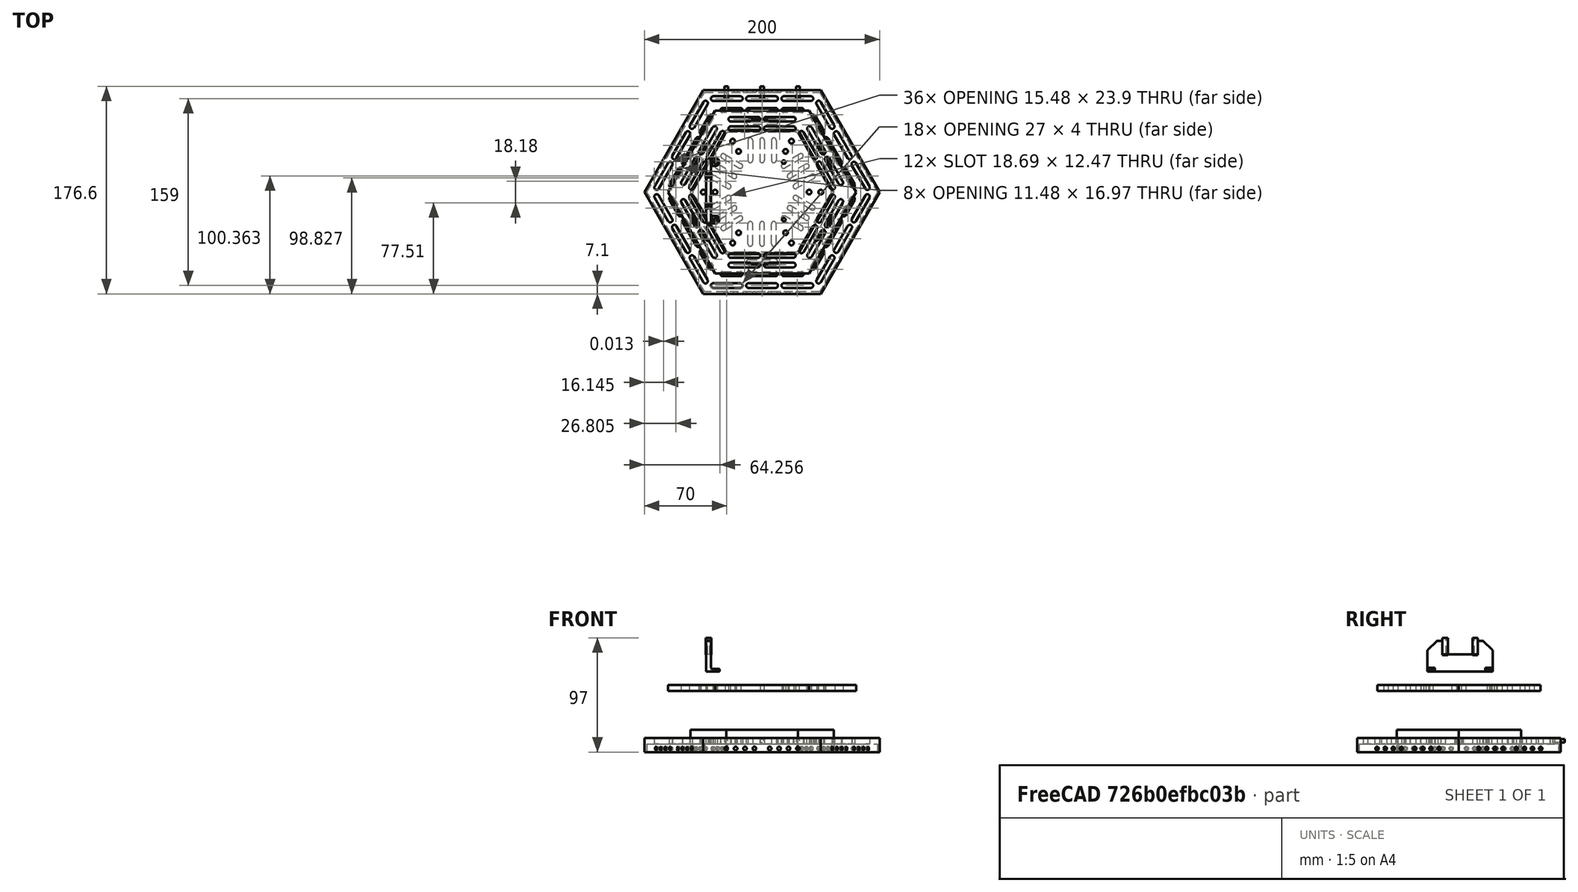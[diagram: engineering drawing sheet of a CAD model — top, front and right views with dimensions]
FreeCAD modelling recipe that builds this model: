
FCSTD DOCUMENT  (FreeCAD 0.16R)
Label: printable_ein
License: All rights reserved
LicenseURL: http://en.wikipedia.org/wiki/All_rights_reserved
objects: Part::Cylinder×299, Part::MultiFuse×130, Part::Box×90, Part::Cut×11, Part::Extrusion×6, Part::RegularPolygon×5, Part::Chamfer×5, App::MeasureDistance×2, Part::Fillet×2, Mesh::Feature×1
note: 548 computed .brp shape members not serialized (recipe doc carries the construction recipe); baked Part::Feature solids carry a one-line shape summary decoded from their .brp

FEATURE [Part::RegularPolygon] RegularPolygon  label="Polígono regular"
  Circumradius = 100
  Polygon = 6
FEATURE [Part::Extrusion] Extrude
  Base = -> RegularPolygon
  Dir = (0,0,12)
  Placement = pos=(0,0,-5) rot=(0,0,1;0rad)
  Solid = true
FEATURE [Part::RegularPolygon] RegularPolygon001  label="Polígono regular001"
  Circumradius = 61
  Polygon = 6
FEATURE [Part::Extrusion] Extrude001
  Base = -> RegularPolygon001
  Dir = (0,0,12)
  Solid = true
FEATURE [Part::Extrusion] Extrude002
  Base = -> RegularPolygon001
  Dir = (0,0,12)
  Solid = true
FEATURE [Part::RegularPolygon] RegularPolygon002  label="Polígono regular002"
  Circumradius = 59
  Polygon = 6
FEATURE [Part::Extrusion] Extrude003
  Base = -> RegularPolygon002
  Dir = (0,0,12)
  Solid = true
FEATURE [Part::Cut] Cut
  Base = -> Extrude002
  Tool = -> Extrude003
FEATURE [Part::RegularPolygon] RegularPolygon003  label="Polígono regular003"
  Circumradius = 98
  Polygon = 6
FEATURE [Part::Extrusion] Extrude004
  Base = -> RegularPolygon003
  Dir = (0,0,12)
  Solid = true
FEATURE [Part::Cut] Cut001
  Base = -> Extrude004
  Tool = -> Cut
FEATURE [Part::Cut] Cut002
  Base = -> Extrude
  Tool = -> Cut001
FEATURE [App::MeasureDistance] Distance  label="Distance: 65.9391 mm"
  Distance = 65.9391
  P1 = (-65.9695,0.0527623,7)
  P2 = (-33,57.1577,7)
FEATURE [App::MeasureDistance] Distance001  label="Distance: 99.9869 mm"
  Distance = 99.9869
  P1 = (-99.9935,0.0113197,7)
  P2 = (-50,86.6025,7)
FEATURE [Part::Cylinder] Cylinder  label="Cilindro"
  Angle = 360
  Height = 10
  Placement = pos=(0,90,2.5) rot=(1,0,0;1.5708rad)
  Radius = 1.5
FEATURE [Part::Cylinder] Cylinder001  label="Cilindro001"
  Angle = 360
  Height = 10
  Placement = pos=(6.5,90,2.5) rot=(1,0,0;1.5708rad)
  Radius = 1.5
FEATURE [Part::Cylinder] Cylinder002  label="Cilindro002"
  Angle = 360
  Height = 10
  Placement = pos=(14.5,90,2.5) rot=(1,0,0;1.5708rad)
  Radius = 1.5
FEATURE [Part::Cylinder] Cylinder003  label="Cilindro003"
  Angle = 360
  Height = 10
  Placement = pos=(14.5,90,2.5) rot=(1,0,0;1.5708rad)
  Radius = 1.5
FEATURE [Part::Cylinder] Cylinder004  label="Cilindro004"
  Angle = 360
  Height = 10
  Placement = pos=(22.5,90,2.5) rot=(1,0,0;1.5708rad)
  Radius = 1.5
FEATURE [Part::Cylinder] Cylinder005  label="Cilindro005"
  Angle = 360
  Height = 10
  Placement = pos=(30.5,90,2.5) rot=(1,0,0;1.5708rad)
  Radius = 1.5
FEATURE [Part::Cylinder] Cylinder006  label="Cilindro006"
  Angle = 360
  Height = 10
  Placement = pos=(-6.5,90,2.5) rot=(1,0,0;1.5708rad)
  Radius = 1.5
FEATURE [Part::Cylinder] Cylinder007  label="Cilindro007"
  Angle = 360
  Height = 10
  Placement = pos=(-14.5,90,2.5) rot=(1,0,0;1.5708rad)
  Radius = 1.5
FEATURE [Part::Cylinder] Cylinder008  label="Cilindro008"
  Angle = 360
  Height = 10
  Placement = pos=(-22.5,90,2.5) rot=(1,0,0;1.5708rad)
  Radius = 1.5
FEATURE [Part::Cylinder] Cylinder009  label="Cilindro009"
  Angle = 360
  Height = 10
  Placement = pos=(-30.5,90,2.5) rot=(1,0,0;1.5708rad)
  Radius = 1.5
FEATURE [Part::MultiFuse] Fusion
  Shapes = -> [Cylinder009,Cylinder008,Cylinder007,Cylinder006,Cylinder005,Cylinder003,Cylinder004,Cylinder002,Cylinder001]
FEATURE [Part::Cylinder] Cylinder010  label="Cilindro010"
  Angle = 360
  Height = 10
  Placement = pos=(6.5,90,2.5) rot=(1,0,0;1.5708rad)
  Radius = 1.5
FEATURE [Part::Cylinder] Cylinder011  label="Cilindro011"
  Angle = 360
  Height = 10
  Placement = pos=(14.5,90,2.5) rot=(1,0,0;1.5708rad)
  Radius = 1.5
FEATURE [Part::Cylinder] Cylinder012  label="Cilindro012"
  Angle = 360
  Height = 10
  Placement = pos=(14.5,90,2.5) rot=(1,0,0;1.5708rad)
  Radius = 1.5
FEATURE [Part::Cylinder] Cylinder013  label="Cilindro013"
  Angle = 360
  Height = 10
  Placement = pos=(22.5,90,2.5) rot=(1,0,0;1.5708rad)
  Radius = 1.5
FEATURE [Part::Cylinder] Cylinder014  label="Cilindro014"
  Angle = 360
  Height = 10
  Placement = pos=(30.5,90,2.5) rot=(1,0,0;1.5708rad)
  Radius = 1.5
FEATURE [Part::Cylinder] Cylinder015  label="Cilindro015"
  Angle = 360
  Height = 10
  Placement = pos=(-6.5,90,2.5) rot=(1,0,0;1.5708rad)
  Radius = 1.5
FEATURE [Part::Cylinder] Cylinder016  label="Cilindro016"
  Angle = 360
  Height = 10
  Placement = pos=(-14.5,90,2.5) rot=(1,0,0;1.5708rad)
  Radius = 1.5
FEATURE [Part::Cylinder] Cylinder017  label="Cilindro017"
  Angle = 360
  Height = 10
  Placement = pos=(-22.5,90,2.5) rot=(1,0,0;1.5708rad)
  Radius = 1.5
FEATURE [Part::Cylinder] Cylinder018  label="Cilindro018"
  Angle = 360
  Height = 10
  Placement = pos=(-30.5,90,2.5) rot=(1,0,0;1.5708rad)
  Radius = 1.5
FEATURE [Part::MultiFuse] Fusion001
  Placement = pos=(0,-29,0) rot=(0,0,1;0rad)
  Shapes = -> [Cylinder017,Cylinder016,Cylinder015,Cylinder012,Cylinder013,Cylinder011,Cylinder010]
FEATURE [Part::MultiFuse] Fusion002
  Shapes = -> [Fusion,Fusion001]
FEATURE [Part::Cylinder] Cylinder019  label="Cilindro019"
  Angle = 360
  Height = 10
  Placement = pos=(6.5,90,2.5) rot=(1,0,0;1.5708rad)
  Radius = 1.5
FEATURE [Part::Cylinder] Cylinder020  label="Cilindro020"
  Angle = 360
  Height = 10
  Placement = pos=(14.5,90,2.5) rot=(1,0,0;1.5708rad)
  Radius = 1.5
FEATURE [Part::Cylinder] Cylinder021  label="Cilindro021"
  Angle = 360
  Height = 10
  Placement = pos=(14.5,90,2.5) rot=(1,0,0;1.5708rad)
  Radius = 1.5
FEATURE [Part::Cylinder] Cylinder022  label="Cilindro022"
  Angle = 360
  Height = 10
  Placement = pos=(22.5,90,2.5) rot=(1,0,0;1.5708rad)
  Radius = 1.5
FEATURE [Part::Cylinder] Cylinder023  label="Cilindro023"
  Angle = 360
  Height = 10
  Placement = pos=(30.5,90,2.5) rot=(1,0,0;1.5708rad)
  Radius = 1.5
FEATURE [Part::Cylinder] Cylinder024  label="Cilindro024"
  Angle = 360
  Height = 10
  Placement = pos=(-6.5,90,2.5) rot=(1,0,0;1.5708rad)
  Radius = 1.5
FEATURE [Part::Cylinder] Cylinder025  label="Cilindro025"
  Angle = 360
  Height = 10
  Placement = pos=(-14.5,90,2.5) rot=(1,0,0;1.5708rad)
  Radius = 1.5
FEATURE [Part::Cylinder] Cylinder026  label="Cilindro026"
  Angle = 360
  Height = 10
  Placement = pos=(-22.5,90,2.5) rot=(1,0,0;1.5708rad)
  Radius = 1.5
FEATURE [Part::Cylinder] Cylinder027  label="Cilindro027"
  Angle = 360
  Height = 10
  Placement = pos=(-30.5,90,2.5) rot=(1,0,0;1.5708rad)
  Radius = 1.5
FEATURE [Part::MultiFuse] Fusion003
  Shapes = -> [Cylinder027,Cylinder026,Cylinder025,Cylinder024,Cylinder023,Cylinder021,Cylinder022,Cylinder020,Cylinder019]
FEATURE [Part::Cylinder] Cylinder028  label="Cilindro028"
  Angle = 360
  Height = 10
  Placement = pos=(6.5,90,2.5) rot=(1,0,0;1.5708rad)
  Radius = 1.5
FEATURE [Part::Cylinder] Cylinder029  label="Cilindro029"
  Angle = 360
  Height = 10
  Placement = pos=(14.5,90,2.5) rot=(1,0,0;1.5708rad)
  Radius = 1.5
FEATURE [Part::Cylinder] Cylinder030  label="Cilindro030"
  Angle = 360
  Height = 10
  Placement = pos=(14.5,90,2.5) rot=(1,0,0;1.5708rad)
  Radius = 1.5
FEATURE [Part::Cylinder] Cylinder031  label="Cilindro031"
  Angle = 360
  Height = 10
  Placement = pos=(22.5,90,2.5) rot=(1,0,0;1.5708rad)
  Radius = 1.5
FEATURE [Part::Cylinder] Cylinder032  label="Cilindro032"
  Angle = 360
  Height = 10
  Placement = pos=(-6.5,90,2.5) rot=(1,0,0;1.5708rad)
  Radius = 1.5
FEATURE [Part::Cylinder] Cylinder033  label="Cilindro033"
  Angle = 360
  Height = 10
  Placement = pos=(-14.5,90,2.5) rot=(1,0,0;1.5708rad)
  Radius = 1.5
FEATURE [Part::Cylinder] Cylinder034  label="Cilindro034"
  Angle = 360
  Height = 10
  Placement = pos=(-22.5,90,2.5) rot=(1,0,0;1.5708rad)
  Radius = 1.5
FEATURE [Part::MultiFuse] Fusion004
  Placement = pos=(0,-29,0) rot=(0,0,1;0rad)
  Shapes = -> [Cylinder034,Cylinder033,Cylinder032,Cylinder030,Cylinder031,Cylinder029,Cylinder028]
FEATURE [Part::MultiFuse] Fusion005
  Placement = pos=(0,0,0) rot=(0,0,1;1.0472rad)
  Shapes = -> [Fusion003,Fusion004]
FEATURE [Part::Cylinder] Cylinder035  label="Cilindro035"
  Angle = 360
  Height = 10
  Placement = pos=(6.5,90,2.5) rot=(1,0,0;1.5708rad)
  Radius = 1.5
FEATURE [Part::Cylinder] Cylinder036  label="Cilindro036"
  Angle = 360
  Height = 10
  Placement = pos=(14.5,90,2.5) rot=(1,0,0;1.5708rad)
  Radius = 1.5
FEATURE [Part::Cylinder] Cylinder037  label="Cilindro037"
  Angle = 360
  Height = 10
  Placement = pos=(14.5,90,2.5) rot=(1,0,0;1.5708rad)
  Radius = 1.5
FEATURE [Part::Cylinder] Cylinder038  label="Cilindro038"
  Angle = 360
  Height = 10
  Placement = pos=(22.5,90,2.5) rot=(1,0,0;1.5708rad)
  Radius = 1.5
FEATURE [Part::Cylinder] Cylinder039  label="Cilindro039"
  Angle = 360
  Height = 10
  Placement = pos=(30.5,90,2.5) rot=(1,0,0;1.5708rad)
  Radius = 1.5
FEATURE [Part::Cylinder] Cylinder040  label="Cilindro040"
  Angle = 360
  Height = 10
  Placement = pos=(-6.5,90,2.5) rot=(1,0,0;1.5708rad)
  Radius = 1.5
FEATURE [Part::Cylinder] Cylinder041  label="Cilindro041"
  Angle = 360
  Height = 10
  Placement = pos=(-14.5,90,2.5) rot=(1,0,0;1.5708rad)
  Radius = 1.5
FEATURE [Part::Cylinder] Cylinder042  label="Cilindro042"
  Angle = 360
  Height = 10
  Placement = pos=(-22.5,90,2.5) rot=(1,0,0;1.5708rad)
  Radius = 1.5
FEATURE [Part::Cylinder] Cylinder043  label="Cilindro043"
  Angle = 360
  Height = 10
  Placement = pos=(-30.5,90,2.5) rot=(1,0,0;1.5708rad)
  Radius = 1.5
FEATURE [Part::MultiFuse] Fusion006
  Shapes = -> [Cylinder043,Cylinder042,Cylinder041,Cylinder040,Cylinder039,Cylinder037,Cylinder038,Cylinder036,Cylinder035]
FEATURE [Part::Cylinder] Cylinder044  label="Cilindro044"
  Angle = 360
  Height = 10
  Placement = pos=(6.5,90,2.5) rot=(1,0,0;1.5708rad)
  Radius = 1.5
FEATURE [Part::Cylinder] Cylinder045  label="Cilindro045"
  Angle = 360
  Height = 10
  Placement = pos=(14.5,90,2.5) rot=(1,0,0;1.5708rad)
  Radius = 1.5
FEATURE [Part::Cylinder] Cylinder046  label="Cilindro046"
  Angle = 360
  Height = 10
  Placement = pos=(14.5,90,2.5) rot=(1,0,0;1.5708rad)
  Radius = 1.5
FEATURE [Part::Cylinder] Cylinder047  label="Cilindro047"
  Angle = 360
  Height = 10
  Placement = pos=(22.5,90,2.5) rot=(1,0,0;1.5708rad)
  Radius = 1.5
FEATURE [Part::Cylinder] Cylinder048  label="Cilindro048"
  Angle = 360
  Height = 10
  Placement = pos=(-6.5,90,2.5) rot=(1,0,0;1.5708rad)
  Radius = 1.5
FEATURE [Part::Cylinder] Cylinder049  label="Cilindro049"
  Angle = 360
  Height = 10
  Placement = pos=(-14.5,90,2.5) rot=(1,0,0;1.5708rad)
  Radius = 1.5
FEATURE [Part::Cylinder] Cylinder050  label="Cilindro050"
  Angle = 360
  Height = 10
  Placement = pos=(-22.5,90,2.5) rot=(1,0,0;1.5708rad)
  Radius = 1.5
FEATURE [Part::MultiFuse] Fusion007
  Placement = pos=(0,-29,0) rot=(0,0,1;0rad)
  Shapes = -> [Cylinder050,Cylinder049,Cylinder048,Cylinder046,Cylinder047,Cylinder045,Cylinder044]
FEATURE [Part::MultiFuse] Fusion008
  Placement = pos=(0,0,0) rot=(0,0,1;2.0944rad)
  Shapes = -> [Fusion006,Fusion007]
FEATURE [Part::Cylinder] Cylinder051  label="Cilindro051"
  Angle = 360
  Height = 10
  Placement = pos=(6.5,90,2.5) rot=(1,0,0;1.5708rad)
  Radius = 1.5
FEATURE [Part::Cylinder] Cylinder052  label="Cilindro052"
  Angle = 360
  Height = 10
  Placement = pos=(14.5,90,2.5) rot=(1,0,0;1.5708rad)
  Radius = 1.5
FEATURE [Part::Cylinder] Cylinder053  label="Cilindro053"
  Angle = 360
  Height = 10
  Placement = pos=(14.5,90,2.5) rot=(1,0,0;1.5708rad)
  Radius = 1.5
FEATURE [Part::Cylinder] Cylinder054  label="Cilindro054"
  Angle = 360
  Height = 10
  Placement = pos=(22.5,90,2.5) rot=(1,0,0;1.5708rad)
  Radius = 1.5
FEATURE [Part::Cylinder] Cylinder055  label="Cilindro055"
  Angle = 360
  Height = 10
  Placement = pos=(30.5,90,2.5) rot=(1,0,0;1.5708rad)
  Radius = 1.5
FEATURE [Part::Cylinder] Cylinder056  label="Cilindro056"
  Angle = 360
  Height = 10
  Placement = pos=(-6.5,90,2.5) rot=(1,0,0;1.5708rad)
  Radius = 1.5
FEATURE [Part::Cylinder] Cylinder057  label="Cilindro057"
  Angle = 360
  Height = 10
  Placement = pos=(-14.5,90,2.5) rot=(1,0,0;1.5708rad)
  Radius = 1.5
FEATURE [Part::Cylinder] Cylinder058  label="Cilindro058"
  Angle = 360
  Height = 10
  Placement = pos=(-22.5,90,2.5) rot=(1,0,0;1.5708rad)
  Radius = 1.5
FEATURE [Part::Cylinder] Cylinder059  label="Cilindro059"
  Angle = 360
  Height = 10
  Placement = pos=(-30.5,90,2.5) rot=(1,0,0;1.5708rad)
  Radius = 1.5
FEATURE [Part::MultiFuse] Fusion009
  Shapes = -> [Cylinder059,Cylinder058,Cylinder057,Cylinder056,Cylinder055,Cylinder053,Cylinder054,Cylinder052,Cylinder051]
FEATURE [Part::Cylinder] Cylinder060  label="Cilindro060"
  Angle = 360
  Height = 10
  Placement = pos=(6.5,90,2.5) rot=(1,0,0;1.5708rad)
  Radius = 1.5
FEATURE [Part::Cylinder] Cylinder061  label="Cilindro061"
  Angle = 360
  Height = 10
  Placement = pos=(14.5,90,2.5) rot=(1,0,0;1.5708rad)
  Radius = 1.5
FEATURE [Part::Cylinder] Cylinder062  label="Cilindro062"
  Angle = 360
  Height = 10
  Placement = pos=(14.5,90,2.5) rot=(1,0,0;1.5708rad)
  Radius = 1.5
FEATURE [Part::Cylinder] Cylinder063  label="Cilindro063"
  Angle = 360
  Height = 10
  Placement = pos=(22.5,90,2.5) rot=(1,0,0;1.5708rad)
  Radius = 1.5
FEATURE [Part::Cylinder] Cylinder064  label="Cilindro064"
  Angle = 360
  Height = 10
  Placement = pos=(-6.5,90,2.5) rot=(1,0,0;1.5708rad)
  Radius = 1.5
FEATURE [Part::Cylinder] Cylinder065  label="Cilindro065"
  Angle = 360
  Height = 10
  Placement = pos=(-14.5,90,2.5) rot=(1,0,0;1.5708rad)
  Radius = 1.5
FEATURE [Part::Cylinder] Cylinder066  label="Cilindro066"
  Angle = 360
  Height = 10
  Placement = pos=(-22.5,90,2.5) rot=(1,0,0;1.5708rad)
  Radius = 1.5
FEATURE [Part::MultiFuse] Fusion010
  Placement = pos=(0,-29,0) rot=(0,0,1;0rad)
  Shapes = -> [Cylinder066,Cylinder065,Cylinder064,Cylinder062,Cylinder063,Cylinder061,Cylinder060]
FEATURE [Part::MultiFuse] Fusion011
  Placement = pos=(0,0,0) rot=(0,0,1;3.14159rad)
  Shapes = -> [Fusion009,Fusion010]
FEATURE [Part::Cylinder] Cylinder067  label="Cilindro067"
  Angle = 360
  Height = 10
  Placement = pos=(6.5,90,2.5) rot=(1,0,0;1.5708rad)
  Radius = 1.5
FEATURE [Part::Cylinder] Cylinder068  label="Cilindro068"
  Angle = 360
  Height = 10
  Placement = pos=(14.5,90,2.5) rot=(1,0,0;1.5708rad)
  Radius = 1.5
FEATURE [Part::Cylinder] Cylinder069  label="Cilindro069"
  Angle = 360
  Height = 10
  Placement = pos=(14.5,90,2.5) rot=(1,0,0;1.5708rad)
  Radius = 1.5
FEATURE [Part::Cylinder] Cylinder070  label="Cilindro070"
  Angle = 360
  Height = 10
  Placement = pos=(22.5,90,2.5) rot=(1,0,0;1.5708rad)
  Radius = 1.5
FEATURE [Part::Cylinder] Cylinder071  label="Cilindro071"
  Angle = 360
  Height = 10
  Placement = pos=(30.5,90,2.5) rot=(1,0,0;1.5708rad)
  Radius = 1.5
FEATURE [Part::Cylinder] Cylinder072  label="Cilindro072"
  Angle = 360
  Height = 10
  Placement = pos=(-6.5,90,2.5) rot=(1,0,0;1.5708rad)
  Radius = 1.5
FEATURE [Part::Cylinder] Cylinder073  label="Cilindro073"
  Angle = 360
  Height = 10
  Placement = pos=(-14.5,90,2.5) rot=(1,0,0;1.5708rad)
  Radius = 1.5
FEATURE [Part::Cylinder] Cylinder074  label="Cilindro074"
  Angle = 360
  Height = 10
  Placement = pos=(-22.5,90,2.5) rot=(1,0,0;1.5708rad)
  Radius = 1.5
FEATURE [Part::Cylinder] Cylinder075  label="Cilindro075"
  Angle = 360
  Height = 10
  Placement = pos=(-30.5,90,2.5) rot=(1,0,0;1.5708rad)
  Radius = 1.5
FEATURE [Part::MultiFuse] Fusion012
  Shapes = -> [Cylinder075,Cylinder074,Cylinder073,Cylinder072,Cylinder071,Cylinder069,Cylinder070,Cylinder068,Cylinder067]
FEATURE [Part::Cylinder] Cylinder076  label="Cilindro076"
  Angle = 360
  Height = 10
  Placement = pos=(6.5,90,2.5) rot=(1,0,0;1.5708rad)
  Radius = 1.5
FEATURE [Part::Cylinder] Cylinder077  label="Cilindro077"
  Angle = 360
  Height = 10
  Placement = pos=(14.5,90,2.5) rot=(1,0,0;1.5708rad)
  Radius = 1.5
FEATURE [Part::Cylinder] Cylinder078  label="Cilindro078"
  Angle = 360
  Height = 10
  Placement = pos=(14.5,90,2.5) rot=(1,0,0;1.5708rad)
  Radius = 1.5
FEATURE [Part::Cylinder] Cylinder079  label="Cilindro079"
  Angle = 360
  Height = 10
  Placement = pos=(22.5,90,2.5) rot=(1,0,0;1.5708rad)
  Radius = 1.5
FEATURE [Part::Cylinder] Cylinder080  label="Cilindro080"
  Angle = 360
  Height = 10
  Placement = pos=(-6.5,90,2.5) rot=(1,0,0;1.5708rad)
  Radius = 1.5
FEATURE [Part::Cylinder] Cylinder081  label="Cilindro081"
  Angle = 360
  Height = 10
  Placement = pos=(-14.5,90,2.5) rot=(1,0,0;1.5708rad)
  Radius = 1.5
FEATURE [Part::Cylinder] Cylinder082  label="Cilindro082"
  Angle = 360
  Height = 10
  Placement = pos=(-22.5,90,2.5) rot=(1,0,0;1.5708rad)
  Radius = 1.5
FEATURE [Part::MultiFuse] Fusion013
  Placement = pos=(0,-29,0) rot=(0,0,1;0rad)
  Shapes = -> [Cylinder082,Cylinder081,Cylinder080,Cylinder078,Cylinder079,Cylinder077,Cylinder076]
FEATURE [Part::MultiFuse] Fusion014
  Placement = pos=(0,0,0) rot=(0,0,-1;1.0472rad)
  Shapes = -> [Fusion012,Fusion013]
FEATURE [Part::Cylinder] Cylinder083  label="Cilindro083"
  Angle = 360
  Height = 10
  Placement = pos=(6.5,90,2.5) rot=(1,0,0;1.5708rad)
  Radius = 1.5
FEATURE [Part::Cylinder] Cylinder084  label="Cilindro084"
  Angle = 360
  Height = 10
  Placement = pos=(14.5,90,2.5) rot=(1,0,0;1.5708rad)
  Radius = 1.5
FEATURE [Part::Cylinder] Cylinder085  label="Cilindro085"
  Angle = 360
  Height = 10
  Placement = pos=(14.5,90,2.5) rot=(1,0,0;1.5708rad)
  Radius = 1.5
FEATURE [Part::Cylinder] Cylinder086  label="Cilindro086"
  Angle = 360
  Height = 10
  Placement = pos=(22.5,90,2.5) rot=(1,0,0;1.5708rad)
  Radius = 1.5
FEATURE [Part::Cylinder] Cylinder087  label="Cilindro087"
  Angle = 360
  Height = 10
  Placement = pos=(30.5,90,2.5) rot=(1,0,0;1.5708rad)
  Radius = 1.5
FEATURE [Part::Cylinder] Cylinder088  label="Cilindro088"
  Angle = 360
  Height = 10
  Placement = pos=(-6.5,90,2.5) rot=(1,0,0;1.5708rad)
  Radius = 1.5
FEATURE [Part::Cylinder] Cylinder089  label="Cilindro089"
  Angle = 360
  Height = 10
  Placement = pos=(-14.5,90,2.5) rot=(1,0,0;1.5708rad)
  Radius = 1.5
FEATURE [Part::Cylinder] Cylinder090  label="Cilindro090"
  Angle = 360
  Height = 10
  Placement = pos=(-22.5,90,2.5) rot=(1,0,0;1.5708rad)
  Radius = 1.5
FEATURE [Part::Cylinder] Cylinder091  label="Cilindro091"
  Angle = 360
  Height = 10
  Placement = pos=(-30.5,90,2.5) rot=(1,0,0;1.5708rad)
  Radius = 1.5
FEATURE [Part::MultiFuse] Fusion015
  Shapes = -> [Cylinder091,Cylinder090,Cylinder089,Cylinder088,Cylinder087,Cylinder085,Cylinder086,Cylinder084,Cylinder083]
FEATURE [Part::Cylinder] Cylinder092  label="Cilindro092"
  Angle = 360
  Height = 10
  Placement = pos=(6.5,90,2.5) rot=(1,0,0;1.5708rad)
  Radius = 1.5
FEATURE [Part::Cylinder] Cylinder093  label="Cilindro093"
  Angle = 360
  Height = 10
  Placement = pos=(14.5,90,2.5) rot=(1,0,0;1.5708rad)
  Radius = 1.5
FEATURE [Part::Cylinder] Cylinder094  label="Cilindro094"
  Angle = 360
  Height = 10
  Placement = pos=(14.5,90,2.5) rot=(1,0,0;1.5708rad)
  Radius = 1.5
FEATURE [Part::Cylinder] Cylinder095  label="Cilindro095"
  Angle = 360
  Height = 10
  Placement = pos=(22.5,90,2.5) rot=(1,0,0;1.5708rad)
  Radius = 1.5
FEATURE [Part::Cylinder] Cylinder096  label="Cilindro096"
  Angle = 360
  Height = 10
  Placement = pos=(-6.5,90,2.5) rot=(1,0,0;1.5708rad)
  Radius = 1.5
FEATURE [Part::Cylinder] Cylinder097  label="Cilindro097"
  Angle = 360
  Height = 10
  Placement = pos=(-14.5,90,2.5) rot=(1,0,0;1.5708rad)
  Radius = 1.5
FEATURE [Part::Cylinder] Cylinder098  label="Cilindro098"
  Angle = 360
  Height = 10
  Placement = pos=(-22.5,90,2.5) rot=(1,0,0;1.5708rad)
  Radius = 1.5
FEATURE [Part::MultiFuse] Fusion016
  Placement = pos=(0,-29,0) rot=(0,0,1;0rad)
  Shapes = -> [Cylinder098,Cylinder097,Cylinder096,Cylinder094,Cylinder095,Cylinder093,Cylinder092]
FEATURE [Part::MultiFuse] Fusion017
  Placement = pos=(0,0,0) rot=(0,0,-1;2.0944rad)
  Shapes = -> [Fusion015,Fusion016]
FEATURE [Part::MultiFuse] Fusion018
  Placement = pos=(0,0,1.5) rot=(0,0,1;0rad)
  Shapes = -> [Fusion017,Fusion014,Fusion011,Fusion008,Fusion005,Fusion002]
FEATURE [Part::Cut] Cut003
  Base = -> Cut002
  Tool = -> Fusion018
FEATURE [Part::Box] Box  label="Cubo"
  Height = 10
  Length = 23
  Width = 4
FEATURE [Part::Cylinder] Cylinder099  label="Cilindro099"
  Angle = 360
  Height = 10
  Placement = pos=(0,2,0) rot=(0,0,1;0rad)
  Radius = 2
FEATURE [Part::Cylinder] Cylinder100  label="Cilindro100"
  Angle = 360
  Height = 10
  Placement = pos=(23,2,0) rot=(0,0,1;0rad)
  Radius = 2
FEATURE [Part::MultiFuse] Fusion019
  Placement = pos=(-11.5,77.5,0) rot=(0,0,1;0rad)
  Shapes = -> [Cylinder099,Cylinder100,Box]
FEATURE [Part::Box] Box001  label="Cubo001"
  Height = 10
  Length = 23
  Width = 4
FEATURE [Part::Cylinder] Cylinder101  label="Cilindro101"
  Angle = 360
  Height = 10
  Placement = pos=(0,2,0) rot=(0,0,1;0rad)
  Radius = 2
FEATURE [Part::Cylinder] Cylinder102  label="Cilindro102"
  Angle = 360
  Height = 10
  Placement = pos=(23,2,0) rot=(0,0,1;0rad)
  Radius = 2
FEATURE [Part::MultiFuse] Fusion020
  Placement = pos=(-11.5,67.5,0) rot=(0,0,1;0rad)
  Shapes = -> [Cylinder101,Cylinder102,Box001]
FEATURE [Part::Box] Box002  label="Cubo002"
  Height = 10
  Length = 23
  Width = 4
FEATURE [Part::Cylinder] Cylinder103  label="Cilindro103"
  Angle = 360
  Height = 10
  Placement = pos=(0,2,0) rot=(0,0,1;0rad)
  Radius = 2
FEATURE [Part::Cylinder] Cylinder104  label="Cilindro104"
  Angle = 360
  Height = 10
  Placement = pos=(23,2,0) rot=(0,0,1;0rad)
  Radius = 2
FEATURE [Part::MultiFuse] Fusion021
  Placement = pos=(-11.5,57.5,0) rot=(0,0,1;0rad)
  Shapes = -> [Cylinder103,Cylinder104,Box002]
FEATURE [Part::Box] Box003  label="Cubo003"
  Height = 10
  Length = 23
  Width = 4
FEATURE [Part::Cylinder] Cylinder105  label="Cilindro105"
  Angle = 360
  Height = 10
  Placement = pos=(0,2,0) rot=(0,0,1;0rad)
  Radius = 2
FEATURE [Part::Cylinder] Cylinder106  label="Cilindro106"
  Angle = 360
  Height = 10
  Placement = pos=(23,2,0) rot=(0,0,1;0rad)
  Radius = 2
FEATURE [Part::MultiFuse] Fusion022
  Placement = pos=(18.5,77.5,0) rot=(0,0,1;0rad)
  Shapes = -> [Cylinder105,Cylinder106,Box003]
FEATURE [Part::Box] Box004  label="Cubo004"
  Height = 10
  Length = 23
  Width = 4
FEATURE [Part::Cylinder] Cylinder107  label="Cilindro107"
  Angle = 360
  Height = 10
  Placement = pos=(0,2,0) rot=(0,0,1;0rad)
  Radius = 2
FEATURE [Part::Cylinder] Cylinder108  label="Cilindro108"
  Angle = 360
  Height = 10
  Placement = pos=(23,2,0) rot=(0,0,1;0rad)
  Radius = 2
FEATURE [Part::MultiFuse] Fusion023
  Placement = pos=(-41.5,77.5,0) rot=(0,0,1;0rad)
  Shapes = -> [Cylinder107,Cylinder108,Box004]
FEATURE [Mesh::Feature] raspy3b
  Placement = pos=(-43,-27,60) rot=(1,0,0;1.5708rad)
FEATURE [Part::Box] Box005  label="Cubo005"
  Height = 10
  Length = 15
  Width = 4
FEATURE [Part::Cylinder] Cylinder109  label="Cilindro109"
  Angle = 360
  Height = 10
  Placement = pos=(0,2,0) rot=(0,0,1;0rad)
  Radius = 2
FEATURE [Part::Cylinder] Cylinder110  label="Cilindro110"
  Angle = 360
  Height = 10
  Placement = pos=(15,2,0) rot=(0,0,1;0rad)
  Radius = 2
FEATURE [Part::MultiFuse] Fusion024
  Placement = pos=(18.5,67.5,0) rot=(0,0,1;0rad)
  Shapes = -> [Box005,Cylinder110,Cylinder109]
FEATURE [Part::Box] Box006  label="Cubo006"
  Height = 10
  Length = 15
  Width = 4
FEATURE [Part::Cylinder] Cylinder111  label="Cilindro111"
  Angle = 360
  Height = 10
  Placement = pos=(0,2,0) rot=(0,0,1;0rad)
  Radius = 2
FEATURE [Part::Cylinder] Cylinder112  label="Cilindro112"
  Angle = 360
  Height = 10
  Placement = pos=(15,2,0) rot=(0,0,1;0rad)
  Radius = 2
FEATURE [Part::MultiFuse] Fusion025
  Placement = pos=(-33.5,67.5,0) rot=(0,0,1;0rad)
  Shapes = -> [Box006,Cylinder112,Cylinder111]
FEATURE [Part::MultiFuse] Fusion026
  Shapes = -> [Fusion023,Fusion022,Fusion021,Fusion019,Fusion020,Fusion024,Fusion025]
FEATURE [Part::Box] Box007  label="Cubo007"
  Height = 10
  Length = 23
  Width = 4
FEATURE [Part::Cylinder] Cylinder113  label="Cilindro113"
  Angle = 360
  Height = 10
  Placement = pos=(0,2,0) rot=(0,0,1;0rad)
  Radius = 2
FEATURE [Part::Cylinder] Cylinder114  label="Cilindro114"
  Angle = 360
  Height = 10
  Placement = pos=(23,2,0) rot=(0,0,1;0rad)
  Radius = 2
FEATURE [Part::MultiFuse] Fusion027
  Placement = pos=(-11.5,77.5,0) rot=(0,0,1;0rad)
  Shapes = -> [Cylinder113,Cylinder114,Box007]
FEATURE [Part::Box] Box008  label="Cubo008"
  Height = 10
  Length = 23
  Width = 4
FEATURE [Part::Cylinder] Cylinder115  label="Cilindro115"
  Angle = 360
  Height = 10
  Placement = pos=(0,2,0) rot=(0,0,1;0rad)
  Radius = 2
FEATURE [Part::Cylinder] Cylinder116  label="Cilindro116"
  Angle = 360
  Height = 10
  Placement = pos=(23,2,0) rot=(0,0,1;0rad)
  Radius = 2
FEATURE [Part::MultiFuse] Fusion028
  Placement = pos=(-11.5,67.5,0) rot=(0,0,1;0rad)
  Shapes = -> [Cylinder115,Cylinder116,Box008]
FEATURE [Part::Box] Box009  label="Cubo009"
  Height = 10
  Length = 23
  Width = 4
FEATURE [Part::Cylinder] Cylinder117  label="Cilindro117"
  Angle = 360
  Height = 10
  Placement = pos=(0,2,0) rot=(0,0,1;0rad)
  Radius = 2
FEATURE [Part::Cylinder] Cylinder118  label="Cilindro118"
  Angle = 360
  Height = 10
  Placement = pos=(23,2,0) rot=(0,0,1;0rad)
  Radius = 2
FEATURE [Part::MultiFuse] Fusion029
  Placement = pos=(-11.5,57.5,0) rot=(0,0,1;0rad)
  Shapes = -> [Cylinder117,Cylinder118,Box009]
FEATURE [Part::Box] Box010  label="Cubo010"
  Height = 10
  Length = 23
  Width = 4
FEATURE [Part::Cylinder] Cylinder119  label="Cilindro119"
  Angle = 360
  Height = 10
  Placement = pos=(0,2,0) rot=(0,0,1;0rad)
  Radius = 2
FEATURE [Part::Cylinder] Cylinder120  label="Cilindro120"
  Angle = 360
  Height = 10
  Placement = pos=(23,2,0) rot=(0,0,1;0rad)
  Radius = 2
FEATURE [Part::MultiFuse] Fusion030
  Placement = pos=(18.5,77.5,0) rot=(0,0,1;0rad)
  Shapes = -> [Cylinder119,Cylinder120,Box010]
FEATURE [Part::Box] Box011  label="Cubo011"
  Height = 10
  Length = 23
  Width = 4
FEATURE [Part::Cylinder] Cylinder121  label="Cilindro121"
  Angle = 360
  Height = 10
  Placement = pos=(0,2,0) rot=(0,0,1;0rad)
  Radius = 2
FEATURE [Part::Cylinder] Cylinder122  label="Cilindro122"
  Angle = 360
  Height = 10
  Placement = pos=(23,2,0) rot=(0,0,1;0rad)
  Radius = 2
FEATURE [Part::MultiFuse] Fusion031
  Placement = pos=(-41.5,77.5,0) rot=(0,0,1;0rad)
  Shapes = -> [Cylinder121,Cylinder122,Box011]
FEATURE [Part::Box] Box012  label="Cubo012"
  Height = 10
  Length = 15
  Width = 4
FEATURE [Part::Cylinder] Cylinder123  label="Cilindro123"
  Angle = 360
  Height = 10
  Placement = pos=(0,2,0) rot=(0,0,1;0rad)
  Radius = 2
FEATURE [Part::Cylinder] Cylinder124  label="Cilindro124"
  Angle = 360
  Height = 10
  Placement = pos=(15,2,0) rot=(0,0,1;0rad)
  Radius = 2
FEATURE [Part::MultiFuse] Fusion032
  Placement = pos=(18.5,67.5,0) rot=(0,0,1;0rad)
  Shapes = -> [Box012,Cylinder124,Cylinder123]
FEATURE [Part::Box] Box013  label="Cubo013"
  Height = 10
  Length = 15
  Width = 4
FEATURE [Part::Cylinder] Cylinder125  label="Cilindro125"
  Angle = 360
  Height = 10
  Placement = pos=(0,2,0) rot=(0,0,1;0rad)
  Radius = 2
FEATURE [Part::Cylinder] Cylinder126  label="Cilindro126"
  Angle = 360
  Height = 10
  Placement = pos=(15,2,0) rot=(0,0,1;0rad)
  Radius = 2
FEATURE [Part::MultiFuse] Fusion033
  Placement = pos=(-33.5,67.5,0) rot=(0,0,1;0rad)
  Shapes = -> [Box013,Cylinder126,Cylinder125]
FEATURE [Part::MultiFuse] Fusion034
  Placement = pos=(0,0,0) rot=(0,0,1;1.0472rad)
  Shapes = -> [Fusion031,Fusion030,Fusion029,Fusion027,Fusion028,Fusion032,Fusion033]
FEATURE [Part::Box] Box014  label="Cubo014"
  Height = 10
  Length = 23
  Width = 4
FEATURE [Part::Cylinder] Cylinder127  label="Cilindro127"
  Angle = 360
  Height = 10
  Placement = pos=(0,2,0) rot=(0,0,1;0rad)
  Radius = 2
FEATURE [Part::Cylinder] Cylinder128  label="Cilindro128"
  Angle = 360
  Height = 10
  Placement = pos=(23,2,0) rot=(0,0,1;0rad)
  Radius = 2
FEATURE [Part::MultiFuse] Fusion035
  Placement = pos=(-11.5,77.5,0) rot=(0,0,1;0rad)
  Shapes = -> [Cylinder127,Cylinder128,Box014]
FEATURE [Part::Box] Box015  label="Cubo015"
  Height = 10
  Length = 23
  Width = 4
FEATURE [Part::Cylinder] Cylinder129  label="Cilindro129"
  Angle = 360
  Height = 10
  Placement = pos=(0,2,0) rot=(0,0,1;0rad)
  Radius = 2
FEATURE [Part::Cylinder] Cylinder130  label="Cilindro130"
  Angle = 360
  Height = 10
  Placement = pos=(23,2,0) rot=(0,0,1;0rad)
  Radius = 2
FEATURE [Part::MultiFuse] Fusion036
  Placement = pos=(-11.5,67.5,0) rot=(0,0,1;0rad)
  Shapes = -> [Cylinder129,Cylinder130,Box015]
FEATURE [Part::Box] Box016  label="Cubo016"
  Height = 10
  Length = 23
  Width = 4
FEATURE [Part::Cylinder] Cylinder131  label="Cilindro131"
  Angle = 360
  Height = 10
  Placement = pos=(0,2,0) rot=(0,0,1;0rad)
  Radius = 2
FEATURE [Part::Cylinder] Cylinder132  label="Cilindro132"
  Angle = 360
  Height = 10
  Placement = pos=(23,2,0) rot=(0,0,1;0rad)
  Radius = 2
FEATURE [Part::MultiFuse] Fusion037
  Placement = pos=(-11.5,57.5,0) rot=(0,0,1;0rad)
  Shapes = -> [Cylinder131,Cylinder132,Box016]
FEATURE [Part::Box] Box017  label="Cubo017"
  Height = 10
  Length = 23
  Width = 4
FEATURE [Part::Cylinder] Cylinder133  label="Cilindro133"
  Angle = 360
  Height = 10
  Placement = pos=(0,2,0) rot=(0,0,1;0rad)
  Radius = 2
FEATURE [Part::Cylinder] Cylinder134  label="Cilindro134"
  Angle = 360
  Height = 10
  Placement = pos=(23,2,0) rot=(0,0,1;0rad)
  Radius = 2
FEATURE [Part::MultiFuse] Fusion038
  Placement = pos=(18.5,77.5,0) rot=(0,0,1;0rad)
  Shapes = -> [Cylinder133,Cylinder134,Box017]
FEATURE [Part::Box] Box018  label="Cubo018"
  Height = 10
  Length = 23
  Width = 4
FEATURE [Part::Cylinder] Cylinder135  label="Cilindro135"
  Angle = 360
  Height = 10
  Placement = pos=(0,2,0) rot=(0,0,1;0rad)
  Radius = 2
FEATURE [Part::Cylinder] Cylinder136  label="Cilindro136"
  Angle = 360
  Height = 10
  Placement = pos=(23,2,0) rot=(0,0,1;0rad)
  Radius = 2
FEATURE [Part::MultiFuse] Fusion039
  Placement = pos=(-41.5,77.5,0) rot=(0,0,1;0rad)
  Shapes = -> [Cylinder135,Cylinder136,Box018]
FEATURE [Part::Box] Box019  label="Cubo019"
  Height = 10
  Length = 15
  Width = 4
FEATURE [Part::Cylinder] Cylinder137  label="Cilindro137"
  Angle = 360
  Height = 10
  Placement = pos=(0,2,0) rot=(0,0,1;0rad)
  Radius = 2
FEATURE [Part::Cylinder] Cylinder138  label="Cilindro138"
  Angle = 360
  Height = 10
  Placement = pos=(15,2,0) rot=(0,0,1;0rad)
  Radius = 2
FEATURE [Part::MultiFuse] Fusion040
  Placement = pos=(18.5,67.5,0) rot=(0,0,1;0rad)
  Shapes = -> [Box019,Cylinder138,Cylinder137]
FEATURE [Part::Box] Box020  label="Cubo020"
  Height = 10
  Length = 15
  Width = 4
FEATURE [Part::Cylinder] Cylinder139  label="Cilindro139"
  Angle = 360
  Height = 10
  Placement = pos=(0,2,0) rot=(0,0,1;0rad)
  Radius = 2
FEATURE [Part::Cylinder] Cylinder140  label="Cilindro140"
  Angle = 360
  Height = 10
  Placement = pos=(15,2,0) rot=(0,0,1;0rad)
  Radius = 2
FEATURE [Part::MultiFuse] Fusion041
  Placement = pos=(-33.5,67.5,0) rot=(0,0,1;0rad)
  Shapes = -> [Box020,Cylinder140,Cylinder139]
FEATURE [Part::MultiFuse] Fusion042
  Placement = pos=(0,0,0) rot=(0,0,-1;1.0472rad)
  Shapes = -> [Fusion039,Fusion038,Fusion037,Fusion035,Fusion036,Fusion040,Fusion041]
FEATURE [Part::Box] Box021  label="Cubo021"
  Height = 10
  Length = 23
  Width = 4
FEATURE [Part::Cylinder] Cylinder141  label="Cilindro141"
  Angle = 360
  Height = 10
  Placement = pos=(0,2,0) rot=(0,0,1;0rad)
  Radius = 2
FEATURE [Part::Cylinder] Cylinder142  label="Cilindro142"
  Angle = 360
  Height = 10
  Placement = pos=(23,2,0) rot=(0,0,1;0rad)
  Radius = 2
FEATURE [Part::MultiFuse] Fusion043
  Placement = pos=(-11.5,77.5,0) rot=(0,0,1;0rad)
  Shapes = -> [Cylinder141,Cylinder142,Box021]
FEATURE [Part::Box] Box022  label="Cubo022"
  Height = 10
  Length = 23
  Width = 4
FEATURE [Part::Cylinder] Cylinder143  label="Cilindro143"
  Angle = 360
  Height = 10
  Placement = pos=(0,2,0) rot=(0,0,1;0rad)
  Radius = 2
FEATURE [Part::Cylinder] Cylinder144  label="Cilindro144"
  Angle = 360
  Height = 10
  Placement = pos=(23,2,0) rot=(0,0,1;0rad)
  Radius = 2
FEATURE [Part::MultiFuse] Fusion044
  Placement = pos=(-11.5,67.5,0) rot=(0,0,1;0rad)
  Shapes = -> [Cylinder143,Cylinder144,Box022]
FEATURE [Part::Box] Box023  label="Cubo023"
  Height = 10
  Length = 23
  Width = 4
FEATURE [Part::Cylinder] Cylinder145  label="Cilindro145"
  Angle = 360
  Height = 10
  Placement = pos=(0,2,0) rot=(0,0,1;0rad)
  Radius = 2
FEATURE [Part::Cylinder] Cylinder146  label="Cilindro146"
  Angle = 360
  Height = 10
  Placement = pos=(23,2,0) rot=(0,0,1;0rad)
  Radius = 2
FEATURE [Part::MultiFuse] Fusion045
  Placement = pos=(-11.5,57.5,0) rot=(0,0,1;0rad)
  Shapes = -> [Cylinder145,Cylinder146,Box023]
FEATURE [Part::Box] Box024  label="Cubo024"
  Height = 10
  Length = 23
  Width = 4
FEATURE [Part::Cylinder] Cylinder147  label="Cilindro147"
  Angle = 360
  Height = 10
  Placement = pos=(0,2,0) rot=(0,0,1;0rad)
  Radius = 2
FEATURE [Part::Cylinder] Cylinder148  label="Cilindro148"
  Angle = 360
  Height = 10
  Placement = pos=(23,2,0) rot=(0,0,1;0rad)
  Radius = 2
FEATURE [Part::MultiFuse] Fusion046
  Placement = pos=(18.5,77.5,0) rot=(0,0,1;0rad)
  Shapes = -> [Cylinder147,Cylinder148,Box024]
FEATURE [Part::Box] Box025  label="Cubo025"
  Height = 10
  Length = 23
  Width = 4
FEATURE [Part::Cylinder] Cylinder149  label="Cilindro149"
  Angle = 360
  Height = 10
  Placement = pos=(0,2,0) rot=(0,0,1;0rad)
  Radius = 2
FEATURE [Part::Cylinder] Cylinder150  label="Cilindro150"
  Angle = 360
  Height = 10
  Placement = pos=(23,2,0) rot=(0,0,1;0rad)
  Radius = 2
FEATURE [Part::MultiFuse] Fusion047
  Placement = pos=(-41.5,77.5,0) rot=(0,0,1;0rad)
  Shapes = -> [Cylinder149,Cylinder150,Box025]
FEATURE [Part::Box] Box026  label="Cubo026"
  Height = 10
  Length = 15
  Width = 4
FEATURE [Part::Cylinder] Cylinder151  label="Cilindro151"
  Angle = 360
  Height = 10
  Placement = pos=(0,2,0) rot=(0,0,1;0rad)
  Radius = 2
FEATURE [Part::Cylinder] Cylinder152  label="Cilindro152"
  Angle = 360
  Height = 10
  Placement = pos=(15,2,0) rot=(0,0,1;0rad)
  Radius = 2
FEATURE [Part::MultiFuse] Fusion048
  Placement = pos=(18.5,67.5,0) rot=(0,0,1;0rad)
  Shapes = -> [Box026,Cylinder152,Cylinder151]
FEATURE [Part::Box] Box027  label="Cubo027"
  Height = 10
  Length = 15
  Width = 4
FEATURE [Part::Cylinder] Cylinder153  label="Cilindro153"
  Angle = 360
  Height = 10
  Placement = pos=(0,2,0) rot=(0,0,1;0rad)
  Radius = 2
FEATURE [Part::Cylinder] Cylinder154  label="Cilindro154"
  Angle = 360
  Height = 10
  Placement = pos=(15,2,0) rot=(0,0,1;0rad)
  Radius = 2
FEATURE [Part::MultiFuse] Fusion049
  Placement = pos=(-33.5,67.5,0) rot=(0,0,1;0rad)
  Shapes = -> [Box027,Cylinder154,Cylinder153]
FEATURE [Part::MultiFuse] Fusion050
  Placement = pos=(0,0,0) rot=(0,0,1;3.14159rad)
  Shapes = -> [Fusion047,Fusion046,Fusion045,Fusion043,Fusion044,Fusion048,Fusion049]
FEATURE [Part::Box] Box028  label="Cubo028"
  Height = 10
  Length = 23
  Width = 4
FEATURE [Part::Cylinder] Cylinder155  label="Cilindro155"
  Angle = 360
  Height = 10
  Placement = pos=(0,2,0) rot=(0,0,1;0rad)
  Radius = 2
FEATURE [Part::Cylinder] Cylinder156  label="Cilindro156"
  Angle = 360
  Height = 10
  Placement = pos=(23,2,0) rot=(0,0,1;0rad)
  Radius = 2
FEATURE [Part::MultiFuse] Fusion051
  Placement = pos=(-11.5,77.5,0) rot=(0,0,1;0rad)
  Shapes = -> [Cylinder155,Cylinder156,Box028]
FEATURE [Part::Box] Box029  label="Cubo029"
  Height = 10
  Length = 23
  Width = 4
FEATURE [Part::Cylinder] Cylinder157  label="Cilindro157"
  Angle = 360
  Height = 10
  Placement = pos=(0,2,0) rot=(0,0,1;0rad)
  Radius = 2
FEATURE [Part::Cylinder] Cylinder158  label="Cilindro158"
  Angle = 360
  Height = 10
  Placement = pos=(23,2,0) rot=(0,0,1;0rad)
  Radius = 2
FEATURE [Part::MultiFuse] Fusion052
  Placement = pos=(-11.5,67.5,0) rot=(0,0,1;0rad)
  Shapes = -> [Cylinder157,Cylinder158,Box029]
FEATURE [Part::Box] Box030  label="Cubo030"
  Height = 10
  Length = 23
  Width = 4
FEATURE [Part::Cylinder] Cylinder159  label="Cilindro159"
  Angle = 360
  Height = 10
  Placement = pos=(0,2,0) rot=(0,0,1;0rad)
  Radius = 2
FEATURE [Part::Cylinder] Cylinder160  label="Cilindro160"
  Angle = 360
  Height = 10
  Placement = pos=(23,2,0) rot=(0,0,1;0rad)
  Radius = 2
FEATURE [Part::MultiFuse] Fusion053
  Placement = pos=(-11.5,57.5,0) rot=(0,0,1;0rad)
  Shapes = -> [Cylinder159,Cylinder160,Box030]
FEATURE [Part::Box] Box031  label="Cubo031"
  Height = 10
  Length = 23
  Width = 4
FEATURE [Part::Cylinder] Cylinder161  label="Cilindro161"
  Angle = 360
  Height = 10
  Placement = pos=(0,2,0) rot=(0,0,1;0rad)
  Radius = 2
FEATURE [Part::Cylinder] Cylinder162  label="Cilindro162"
  Angle = 360
  Height = 10
  Placement = pos=(23,2,0) rot=(0,0,1;0rad)
  Radius = 2
FEATURE [Part::MultiFuse] Fusion054
  Placement = pos=(18.5,77.5,0) rot=(0,0,1;0rad)
  Shapes = -> [Cylinder161,Cylinder162,Box031]
FEATURE [Part::Box] Box032  label="Cubo032"
  Height = 10
  Length = 23
  Width = 4
FEATURE [Part::Cylinder] Cylinder163  label="Cilindro163"
  Angle = 360
  Height = 10
  Placement = pos=(0,2,0) rot=(0,0,1;0rad)
  Radius = 2
FEATURE [Part::Cylinder] Cylinder164  label="Cilindro164"
  Angle = 360
  Height = 10
  Placement = pos=(23,2,0) rot=(0,0,1;0rad)
  Radius = 2
FEATURE [Part::MultiFuse] Fusion055
  Placement = pos=(-41.5,77.5,0) rot=(0,0,1;0rad)
  Shapes = -> [Cylinder163,Cylinder164,Box032]
FEATURE [Part::Box] Box033  label="Cubo033"
  Height = 10
  Length = 15
  Width = 4
FEATURE [Part::Cylinder] Cylinder165  label="Cilindro165"
  Angle = 360
  Height = 10
  Placement = pos=(0,2,0) rot=(0,0,1;0rad)
  Radius = 2
FEATURE [Part::Cylinder] Cylinder166  label="Cilindro166"
  Angle = 360
  Height = 10
  Placement = pos=(15,2,0) rot=(0,0,1;0rad)
  Radius = 2
FEATURE [Part::MultiFuse] Fusion056
  Placement = pos=(18.5,67.5,0) rot=(0,0,1;0rad)
  Shapes = -> [Box033,Cylinder166,Cylinder165]
FEATURE [Part::Box] Box034  label="Cubo034"
  Height = 10
  Length = 15
  Width = 4
FEATURE [Part::Cylinder] Cylinder167  label="Cilindro167"
  Angle = 360
  Height = 10
  Placement = pos=(0,2,0) rot=(0,0,1;0rad)
  Radius = 2
FEATURE [Part::Cylinder] Cylinder168  label="Cilindro168"
  Angle = 360
  Height = 10
  Placement = pos=(15,2,0) rot=(0,0,1;0rad)
  Radius = 2
FEATURE [Part::MultiFuse] Fusion057
  Placement = pos=(-33.5,67.5,0) rot=(0,0,1;0rad)
  Shapes = -> [Box034,Cylinder168,Cylinder167]
FEATURE [Part::MultiFuse] Fusion058
  Placement = pos=(0,0,0) rot=(0,0,1;2.0944rad)
  Shapes = -> [Fusion055,Fusion054,Fusion053,Fusion051,Fusion052,Fusion056,Fusion057]
FEATURE [Part::Box] Box035  label="Cubo035"
  Height = 10
  Length = 23
  Width = 4
FEATURE [Part::Cylinder] Cylinder169  label="Cilindro169"
  Angle = 360
  Height = 10
  Placement = pos=(0,2,0) rot=(0,0,1;0rad)
  Radius = 2
FEATURE [Part::Cylinder] Cylinder170  label="Cilindro170"
  Angle = 360
  Height = 10
  Placement = pos=(23,2,0) rot=(0,0,1;0rad)
  Radius = 2
FEATURE [Part::MultiFuse] Fusion059
  Placement = pos=(-11.5,77.5,0) rot=(0,0,1;0rad)
  Shapes = -> [Cylinder169,Cylinder170,Box035]
FEATURE [Part::Box] Box036  label="Cubo036"
  Height = 10
  Length = 23
  Width = 4
FEATURE [Part::Cylinder] Cylinder171  label="Cilindro171"
  Angle = 360
  Height = 10
  Placement = pos=(0,2,0) rot=(0,0,1;0rad)
  Radius = 2
FEATURE [Part::Cylinder] Cylinder172  label="Cilindro172"
  Angle = 360
  Height = 10
  Placement = pos=(23,2,0) rot=(0,0,1;0rad)
  Radius = 2
FEATURE [Part::MultiFuse] Fusion060
  Placement = pos=(-11.5,67.5,0) rot=(0,0,1;0rad)
  Shapes = -> [Cylinder171,Cylinder172,Box036]
FEATURE [Part::Box] Box037  label="Cubo037"
  Height = 10
  Length = 23
  Width = 4
FEATURE [Part::Cylinder] Cylinder173  label="Cilindro173"
  Angle = 360
  Height = 10
  Placement = pos=(0,2,0) rot=(0,0,1;0rad)
  Radius = 2
FEATURE [Part::Cylinder] Cylinder174  label="Cilindro174"
  Angle = 360
  Height = 10
  Placement = pos=(23,2,0) rot=(0,0,1;0rad)
  Radius = 2
FEATURE [Part::MultiFuse] Fusion061
  Placement = pos=(-11.5,57.5,0) rot=(0,0,1;0rad)
  Shapes = -> [Cylinder173,Cylinder174,Box037]
FEATURE [Part::Box] Box038  label="Cubo038"
  Height = 10
  Length = 23
  Width = 4
FEATURE [Part::Cylinder] Cylinder175  label="Cilindro175"
  Angle = 360
  Height = 10
  Placement = pos=(0,2,0) rot=(0,0,1;0rad)
  Radius = 2
FEATURE [Part::Cylinder] Cylinder176  label="Cilindro176"
  Angle = 360
  Height = 10
  Placement = pos=(23,2,0) rot=(0,0,1;0rad)
  Radius = 2
FEATURE [Part::MultiFuse] Fusion062
  Placement = pos=(18.5,77.5,0) rot=(0,0,1;0rad)
  Shapes = -> [Cylinder175,Cylinder176,Box038]
FEATURE [Part::Box] Box039  label="Cubo039"
  Height = 10
  Length = 23
  Width = 4
FEATURE [Part::Cylinder] Cylinder177  label="Cilindro177"
  Angle = 360
  Height = 10
  Placement = pos=(0,2,0) rot=(0,0,1;0rad)
  Radius = 2
FEATURE [Part::Cylinder] Cylinder178  label="Cilindro178"
  Angle = 360
  Height = 10
  Placement = pos=(23,2,0) rot=(0,0,1;0rad)
  Radius = 2
FEATURE [Part::MultiFuse] Fusion063
  Placement = pos=(-41.5,77.5,0) rot=(0,0,1;0rad)
  Shapes = -> [Cylinder177,Cylinder178,Box039]
FEATURE [Part::Box] Box040  label="Cubo040"
  Height = 10
  Length = 15
  Width = 4
FEATURE [Part::Cylinder] Cylinder179  label="Cilindro179"
  Angle = 360
  Height = 10
  Placement = pos=(0,2,0) rot=(0,0,1;0rad)
  Radius = 2
FEATURE [Part::Cylinder] Cylinder180  label="Cilindro180"
  Angle = 360
  Height = 10
  Placement = pos=(15,2,0) rot=(0,0,1;0rad)
  Radius = 2
FEATURE [Part::MultiFuse] Fusion064
  Placement = pos=(18.5,67.5,0) rot=(0,0,1;0rad)
  Shapes = -> [Box040,Cylinder180,Cylinder179]
FEATURE [Part::Box] Box041  label="Cubo041"
  Height = 10
  Length = 15
  Width = 4
FEATURE [Part::Cylinder] Cylinder181  label="Cilindro181"
  Angle = 360
  Height = 10
  Placement = pos=(0,2,0) rot=(0,0,1;0rad)
  Radius = 2
FEATURE [Part::Cylinder] Cylinder182  label="Cilindro182"
  Angle = 360
  Height = 10
  Placement = pos=(15,2,0) rot=(0,0,1;0rad)
  Radius = 2
FEATURE [Part::MultiFuse] Fusion065
  Placement = pos=(-33.5,67.5,0) rot=(0,0,1;0rad)
  Shapes = -> [Box041,Cylinder182,Cylinder181]
FEATURE [Part::MultiFuse] Fusion066
  Placement = pos=(0,0,0) rot=(0,0,-1;2.0944rad)
  Shapes = -> [Fusion063,Fusion062,Fusion061,Fusion059,Fusion060,Fusion064,Fusion065]
FEATURE [Part::MultiFuse] Fusion067
  Placement = pos=(0,0,-7) rot=(0,0,1;0rad)
  Shapes = -> [Fusion026,Fusion034,Fusion042,Fusion050,Fusion058,Fusion066]
FEATURE [Part::Cut] Cut004
  Base = -> Cut003
  Tool = -> Fusion067
FEATURE [Part::Cylinder] Cylinder183  label="Cilindro183"
  Angle = 360
  Height = 10
  Placement = pos=(25,43.3,0) rot=(0,0,1;0rad)
  Radius = 2
FEATURE [Part::Cylinder] Cylinder184  label="Cilindro184"
  Angle = 360
  Height = 10
  Placement = pos=(20,34.6,0) rot=(0,0,1;0rad)
  Radius = 2
FEATURE [Part::Box] Box042  label="Cubo042"
  Height = 10
  Length = 4
  Width = 17
FEATURE [Part::Cylinder] Cylinder185  label="Cilindro185"
  Angle = 360
  Height = 10
  Placement = pos=(2,0,0) rot=(0,0,1;0rad)
  Radius = 2
FEATURE [Part::Cylinder] Cylinder186  label="Cilindro186"
  Angle = 360
  Height = 10
  Placement = pos=(2,17,0) rot=(0,0,1;0rad)
  Radius = 2
FEATURE [Part::MultiFuse] Fusion068
  Placement = pos=(-2,27,0) rot=(0,0,1;0rad)
  Shapes = -> [Cylinder186,Cylinder185,Box042]
FEATURE [Part::Box] Box043  label="Cubo043"
  Height = 10
  Length = 4
  Width = 17
FEATURE [Part::Cylinder] Cylinder187  label="Cilindro187"
  Angle = 360
  Height = 10
  Placement = pos=(2,0,0) rot=(0,0,1;0rad)
  Radius = 2
FEATURE [Part::Cylinder] Cylinder188  label="Cilindro188"
  Angle = 360
  Height = 10
  Placement = pos=(2,17,0) rot=(0,0,1;0rad)
  Radius = 2
FEATURE [Part::MultiFuse] Fusion069
  Placement = pos=(8,27,0) rot=(0,0,1;0rad)
  Shapes = -> [Cylinder188,Cylinder187,Box043]
FEATURE [Part::Box] Box044  label="Cubo044"
  Height = 10
  Length = 4
  Width = 17
FEATURE [Part::Cylinder] Cylinder189  label="Cilindro189"
  Angle = 360
  Height = 10
  Placement = pos=(2,0,0) rot=(0,0,1;0rad)
  Radius = 2
FEATURE [Part::Cylinder] Cylinder190  label="Cilindro190"
  Angle = 360
  Height = 10
  Placement = pos=(2,17,0) rot=(0,0,1;0rad)
  Radius = 2
FEATURE [Part::MultiFuse] Fusion070
  Placement = pos=(-12,27,0) rot=(0,0,1;0rad)
  Shapes = -> [Cylinder190,Cylinder189,Box044]
FEATURE [Part::MultiFuse] Fusion071
  Shapes = -> [Fusion070,Fusion069,Fusion068,Cylinder184,Cylinder183]
FEATURE [Part::Cylinder] Cylinder191  label="Cilindro191"
  Angle = 360
  Height = 10
  Placement = pos=(25,43.3,0) rot=(0,0,1;0rad)
  Radius = 2
FEATURE [Part::Cylinder] Cylinder192  label="Cilindro192"
  Angle = 360
  Height = 10
  Placement = pos=(20,34.6,0) rot=(0,0,1;0rad)
  Radius = 2
FEATURE [Part::Box] Box045  label="Cubo045"
  Height = 10
  Length = 4
  Width = 17
FEATURE [Part::Cylinder] Cylinder193  label="Cilindro193"
  Angle = 360
  Height = 10
  Placement = pos=(2,0,0) rot=(0,0,1;0rad)
  Radius = 2
FEATURE [Part::Cylinder] Cylinder194  label="Cilindro194"
  Angle = 360
  Height = 10
  Placement = pos=(2,17,0) rot=(0,0,1;0rad)
  Radius = 2
FEATURE [Part::MultiFuse] Fusion072
  Placement = pos=(-2,27,0) rot=(0,0,1;0rad)
  Shapes = -> [Cylinder194,Cylinder193,Box045]
FEATURE [Part::Box] Box046  label="Cubo046"
  Height = 10
  Length = 4
  Width = 17
FEATURE [Part::Cylinder] Cylinder195  label="Cilindro195"
  Angle = 360
  Height = 10
  Placement = pos=(2,0,0) rot=(0,0,1;0rad)
  Radius = 2
FEATURE [Part::Cylinder] Cylinder196  label="Cilindro196"
  Angle = 360
  Height = 10
  Placement = pos=(2,17,0) rot=(0,0,1;0rad)
  Radius = 2
FEATURE [Part::MultiFuse] Fusion073
  Placement = pos=(8,27,0) rot=(0,0,1;0rad)
  Shapes = -> [Cylinder196,Cylinder195,Box046]
FEATURE [Part::Box] Box047  label="Cubo047"
  Height = 10
  Length = 4
  Width = 17
FEATURE [Part::Cylinder] Cylinder197  label="Cilindro197"
  Angle = 360
  Height = 10
  Placement = pos=(2,0,0) rot=(0,0,1;0rad)
  Radius = 2
FEATURE [Part::Cylinder] Cylinder198  label="Cilindro198"
  Angle = 360
  Height = 10
  Placement = pos=(2,17,0) rot=(0,0,1;0rad)
  Radius = 2
FEATURE [Part::MultiFuse] Fusion074
  Placement = pos=(-12,27,0) rot=(0,0,1;0rad)
  Shapes = -> [Cylinder198,Cylinder197,Box047]
FEATURE [Part::MultiFuse] Fusion075
  Placement = pos=(0,0,0) rot=(0,0,1;1.0472rad)
  Shapes = -> [Fusion074,Fusion073,Fusion072,Cylinder192,Cylinder191]
FEATURE [Part::Cylinder] Cylinder199  label="Cilindro199"
  Angle = 360
  Height = 10
  Placement = pos=(25,43.3,0) rot=(0,0,1;0rad)
  Radius = 2
FEATURE [Part::Cylinder] Cylinder200  label="Cilindro200"
  Angle = 360
  Height = 10
  Placement = pos=(20,34.6,0) rot=(0,0,1;0rad)
  Radius = 2
FEATURE [Part::Box] Box048  label="Cubo048"
  Height = 10
  Length = 4
  Width = 17
FEATURE [Part::Cylinder] Cylinder201  label="Cilindro201"
  Angle = 360
  Height = 10
  Placement = pos=(2,0,0) rot=(0,0,1;0rad)
  Radius = 2
FEATURE [Part::Cylinder] Cylinder202  label="Cilindro202"
  Angle = 360
  Height = 10
  Placement = pos=(2,17,0) rot=(0,0,1;0rad)
  Radius = 2
FEATURE [Part::MultiFuse] Fusion076
  Placement = pos=(-2,27,0) rot=(0,0,1;0rad)
  Shapes = -> [Cylinder202,Cylinder201,Box048]
FEATURE [Part::Box] Box049  label="Cubo049"
  Height = 10
  Length = 4
  Width = 17
FEATURE [Part::Cylinder] Cylinder203  label="Cilindro203"
  Angle = 360
  Height = 10
  Placement = pos=(2,0,0) rot=(0,0,1;0rad)
  Radius = 2
FEATURE [Part::Cylinder] Cylinder204  label="Cilindro204"
  Angle = 360
  Height = 10
  Placement = pos=(2,17,0) rot=(0,0,1;0rad)
  Radius = 2
FEATURE [Part::MultiFuse] Fusion077
  Placement = pos=(8,27,0) rot=(0,0,1;0rad)
  Shapes = -> [Cylinder204,Cylinder203,Box049]
FEATURE [Part::Box] Box050  label="Cubo050"
  Height = 10
  Length = 4
  Width = 17
FEATURE [Part::Cylinder] Cylinder205  label="Cilindro205"
  Angle = 360
  Height = 10
  Placement = pos=(2,0,0) rot=(0,0,1;0rad)
  Radius = 2
FEATURE [Part::Cylinder] Cylinder206  label="Cilindro206"
  Angle = 360
  Height = 10
  Placement = pos=(2,17,0) rot=(0,0,1;0rad)
  Radius = 2
FEATURE [Part::MultiFuse] Fusion078
  Placement = pos=(-12,27,0) rot=(0,0,1;0rad)
  Shapes = -> [Cylinder206,Cylinder205,Box050]
FEATURE [Part::MultiFuse] Fusion079
  Placement = pos=(0,0,0) rot=(0,0,1;2.0944rad)
  Shapes = -> [Fusion078,Fusion077,Fusion076,Cylinder200,Cylinder199]
FEATURE [Part::Cylinder] Cylinder207  label="Cilindro207"
  Angle = 360
  Height = 10
  Placement = pos=(25,43.3,0) rot=(0,0,1;0rad)
  Radius = 2
FEATURE [Part::Cylinder] Cylinder208  label="Cilindro208"
  Angle = 360
  Height = 10
  Placement = pos=(20,34.6,0) rot=(0,0,1;0rad)
  Radius = 2
FEATURE [Part::Box] Box051  label="Cubo051"
  Height = 10
  Length = 4
  Width = 17
FEATURE [Part::Cylinder] Cylinder209  label="Cilindro209"
  Angle = 360
  Height = 10
  Placement = pos=(2,0,0) rot=(0,0,1;0rad)
  Radius = 2
FEATURE [Part::Cylinder] Cylinder210  label="Cilindro210"
  Angle = 360
  Height = 10
  Placement = pos=(2,17,0) rot=(0,0,1;0rad)
  Radius = 2
FEATURE [Part::MultiFuse] Fusion080
  Placement = pos=(-2,27,0) rot=(0,0,1;0rad)
  Shapes = -> [Cylinder210,Cylinder209,Box051]
FEATURE [Part::Box] Box052  label="Cubo052"
  Height = 10
  Length = 4
  Width = 17
FEATURE [Part::Cylinder] Cylinder211  label="Cilindro211"
  Angle = 360
  Height = 10
  Placement = pos=(2,0,0) rot=(0,0,1;0rad)
  Radius = 2
FEATURE [Part::Cylinder] Cylinder212  label="Cilindro212"
  Angle = 360
  Height = 10
  Placement = pos=(2,17,0) rot=(0,0,1;0rad)
  Radius = 2
FEATURE [Part::MultiFuse] Fusion081
  Placement = pos=(8,27,0) rot=(0,0,1;0rad)
  Shapes = -> [Cylinder212,Cylinder211,Box052]
FEATURE [Part::Box] Box053  label="Cubo053"
  Height = 10
  Length = 4
  Width = 17
FEATURE [Part::Cylinder] Cylinder213  label="Cilindro213"
  Angle = 360
  Height = 10
  Placement = pos=(2,0,0) rot=(0,0,1;0rad)
  Radius = 2
FEATURE [Part::Cylinder] Cylinder214  label="Cilindro214"
  Angle = 360
  Height = 10
  Placement = pos=(2,17,0) rot=(0,0,1;0rad)
  Radius = 2
FEATURE [Part::MultiFuse] Fusion082
  Placement = pos=(-12,27,0) rot=(0,0,1;0rad)
  Shapes = -> [Cylinder214,Cylinder213,Box053]
FEATURE [Part::MultiFuse] Fusion083
  Placement = pos=(0,0,0) rot=(0,0,1;3.14159rad)
  Shapes = -> [Fusion082,Fusion081,Fusion080,Cylinder208,Cylinder207]
FEATURE [Part::Cylinder] Cylinder215  label="Cilindro215"
  Angle = 360
  Height = 10
  Placement = pos=(25,43.3,0) rot=(0,0,1;0rad)
  Radius = 2
FEATURE [Part::Cylinder] Cylinder216  label="Cilindro216"
  Angle = 360
  Height = 10
  Placement = pos=(20,34.6,0) rot=(0,0,1;0rad)
  Radius = 2
FEATURE [Part::Box] Box054  label="Cubo054"
  Height = 10
  Length = 4
  Width = 17
FEATURE [Part::Cylinder] Cylinder217  label="Cilindro217"
  Angle = 360
  Height = 10
  Placement = pos=(2,0,0) rot=(0,0,1;0rad)
  Radius = 2
FEATURE [Part::Cylinder] Cylinder218  label="Cilindro218"
  Angle = 360
  Height = 10
  Placement = pos=(2,17,0) rot=(0,0,1;0rad)
  Radius = 2
FEATURE [Part::MultiFuse] Fusion084
  Placement = pos=(-2,27,0) rot=(0,0,1;0rad)
  Shapes = -> [Cylinder218,Cylinder217,Box054]
FEATURE [Part::Box] Box055  label="Cubo055"
  Height = 10
  Length = 4
  Width = 17
FEATURE [Part::Cylinder] Cylinder219  label="Cilindro219"
  Angle = 360
  Height = 10
  Placement = pos=(2,0,0) rot=(0,0,1;0rad)
  Radius = 2
FEATURE [Part::Cylinder] Cylinder220  label="Cilindro220"
  Angle = 360
  Height = 10
  Placement = pos=(2,17,0) rot=(0,0,1;0rad)
  Radius = 2
FEATURE [Part::MultiFuse] Fusion085
  Placement = pos=(8,27,0) rot=(0,0,1;0rad)
  Shapes = -> [Cylinder220,Cylinder219,Box055]
FEATURE [Part::Box] Box056  label="Cubo056"
  Height = 10
  Length = 4
  Width = 17
FEATURE [Part::Cylinder] Cylinder221  label="Cilindro221"
  Angle = 360
  Height = 10
  Placement = pos=(2,0,0) rot=(0,0,1;0rad)
  Radius = 2
FEATURE [Part::Cylinder] Cylinder222  label="Cilindro222"
  Angle = 360
  Height = 10
  Placement = pos=(2,17,0) rot=(0,0,1;0rad)
  Radius = 2
FEATURE [Part::MultiFuse] Fusion086
  Placement = pos=(-12,27,0) rot=(0,0,1;0rad)
  Shapes = -> [Cylinder222,Cylinder221,Box056]
FEATURE [Part::MultiFuse] Fusion087
  Placement = pos=(0,0,0) rot=(0,0,-1;1.0472rad)
  Shapes = -> [Fusion086,Fusion085,Fusion084,Cylinder216,Cylinder215]
FEATURE [Part::Cylinder] Cylinder223  label="Cilindro223"
  Angle = 360
  Height = 10
  Placement = pos=(25,43.3,0) rot=(0,0,1;0rad)
  Radius = 2
FEATURE [Part::Cylinder] Cylinder224  label="Cilindro224"
  Angle = 360
  Height = 10
  Placement = pos=(20,34.6,0) rot=(0,0,1;0rad)
  Radius = 2
FEATURE [Part::Box] Box057  label="Cubo057"
  Height = 10
  Length = 4
  Width = 17
FEATURE [Part::Cylinder] Cylinder225  label="Cilindro225"
  Angle = 360
  Height = 10
  Placement = pos=(2,0,0) rot=(0,0,1;0rad)
  Radius = 2
FEATURE [Part::Cylinder] Cylinder226  label="Cilindro226"
  Angle = 360
  Height = 10
  Placement = pos=(2,17,0) rot=(0,0,1;0rad)
  Radius = 2
FEATURE [Part::MultiFuse] Fusion088
  Placement = pos=(-2,27,0) rot=(0,0,1;0rad)
  Shapes = -> [Cylinder226,Cylinder225,Box057]
FEATURE [Part::Box] Box058  label="Cubo058"
  Height = 10
  Length = 4
  Width = 17
FEATURE [Part::Cylinder] Cylinder227  label="Cilindro227"
  Angle = 360
  Height = 10
  Placement = pos=(2,0,0) rot=(0,0,1;0rad)
  Radius = 2
FEATURE [Part::Cylinder] Cylinder228  label="Cilindro228"
  Angle = 360
  Height = 10
  Placement = pos=(2,17,0) rot=(0,0,1;0rad)
  Radius = 2
FEATURE [Part::MultiFuse] Fusion089
  Placement = pos=(8,27,0) rot=(0,0,1;0rad)
  Shapes = -> [Cylinder228,Cylinder227,Box058]
FEATURE [Part::Box] Box059  label="Cubo059"
  Height = 10
  Length = 4
  Width = 17
FEATURE [Part::Cylinder] Cylinder229  label="Cilindro229"
  Angle = 360
  Height = 10
  Placement = pos=(2,0,0) rot=(0,0,1;0rad)
  Radius = 2
FEATURE [Part::Cylinder] Cylinder230  label="Cilindro230"
  Angle = 360
  Height = 10
  Placement = pos=(2,17,0) rot=(0,0,1;0rad)
  Radius = 2
FEATURE [Part::MultiFuse] Fusion090
  Placement = pos=(-12,27,0) rot=(0,0,1;0rad)
  Shapes = -> [Cylinder230,Cylinder229,Box059]
FEATURE [Part::MultiFuse] Fusion091
  Placement = pos=(0,0,0) rot=(0,0,-1;2.0944rad)
  Shapes = -> [Fusion090,Fusion089,Fusion088,Cylinder224,Cylinder223]
FEATURE [Part::MultiFuse] Fusion092
  Placement = pos=(0,0,-7) rot=(0,0,1;0rad)
  Shapes = -> [Fusion091,Fusion087,Fusion083,Fusion075,Fusion079,Fusion071]
FEATURE [Part::Cut] Cut005
  Base = -> Cut004
  Placement = pos=(0,0,0) rot=(1,0,0;3.14159rad)
  Tool = -> Fusion092
FEATURE [Part::RegularPolygon] RegularPolygon004  label="Polígono regular004"
  Circumradius = 80
  Polygon = 6
FEATURE [Part::Extrusion] Extrude005
  Base = -> RegularPolygon004
  Dir = (0,0,5)
  Placement = pos=(0,0,-50) rot=(0,0,1;0rad)
  Solid = true
FEATURE [Part::Cylinder] Cylinder231  label="Cilindro231"
  Angle = 360
  Height = 10
  Placement = pos=(20,34.6,0) rot=(0,0,1;0rad)
  Radius = 2
FEATURE [Part::Cylinder] Cylinder232  label="Cilindro232"
  Angle = 360
  Height = 10
  Placement = pos=(25,43.3,0) rot=(0,0,1;0rad)
  Radius = 2
FEATURE [Part::Box] Box060  label="Cubo060"
  Height = 10
  Length = 23
  Width = 4
FEATURE [Part::Cylinder] Cylinder233  label="Cilindro233"
  Angle = 360
  Height = 10
  Placement = pos=(0,2,0) rot=(0,0,1;0rad)
  Radius = 2
FEATURE [Part::Cylinder] Cylinder234  label="Cilindro234"
  Angle = 360
  Height = 10
  Placement = pos=(23,2,0) rot=(0,0,1;0rad)
  Radius = 2
FEATURE [Part::MultiFuse] Fusion093
  Placement = pos=(3.5,60,0) rot=(0,0,1;0rad)
  Shapes = -> [Box060,Cylinder234,Cylinder233]
FEATURE [Part::Box] Box061  label="Cubo061"
  Height = 10
  Length = 23
  Width = 4
FEATURE [Part::Cylinder] Cylinder235  label="Cilindro235"
  Angle = 360
  Height = 10
  Placement = pos=(0,2,0) rot=(0,0,1;0rad)
  Radius = 2
FEATURE [Part::Cylinder] Cylinder236  label="Cilindro236"
  Angle = 360
  Height = 10
  Placement = pos=(23,2,0) rot=(0,0,1;0rad)
  Radius = 2
FEATURE [Part::MultiFuse] Fusion094
  Placement = pos=(-26.5,60,0) rot=(0,0,1;0rad)
  Shapes = -> [Box061,Cylinder236,Cylinder235]
FEATURE [Part::Box] Box062  label="Cubo062"
  Height = 10
  Length = 23
  Width = 4
FEATURE [Part::Cylinder] Cylinder237  label="Cilindro237"
  Angle = 360
  Height = 10
  Placement = pos=(0,2,0) rot=(0,0,1;0rad)
  Radius = 2
FEATURE [Part::Cylinder] Cylinder238  label="Cilindro238"
  Angle = 360
  Height = 10
  Placement = pos=(23,2,0) rot=(0,0,1;0rad)
  Radius = 2
FEATURE [Part::MultiFuse] Fusion095
  Placement = pos=(3.5,52,0) rot=(0,0,1;0rad)
  Shapes = -> [Box062,Cylinder238,Cylinder237]
FEATURE [Part::Box] Box063  label="Cubo063"
  Height = 10
  Length = 23
  Width = 4
FEATURE [Part::Cylinder] Cylinder239  label="Cilindro239"
  Angle = 360
  Height = 10
  Placement = pos=(0,2,0) rot=(0,0,1;0rad)
  Radius = 2
FEATURE [Part::Cylinder] Cylinder240  label="Cilindro240"
  Angle = 360
  Height = 10
  Placement = pos=(23,2,0) rot=(0,0,1;0rad)
  Radius = 2
FEATURE [Part::MultiFuse] Fusion096
  Placement = pos=(-26.5,52,0) rot=(0,0,1;0rad)
  Shapes = -> [Box063,Cylinder240,Cylinder239]
FEATURE [Part::MultiFuse] Fusion097
  Placement = pos=(0,0,-52) rot=(0,0,1;0rad)
  Shapes = -> [Fusion095,Fusion096,Fusion094,Fusion093,Cylinder232,Cylinder231]
FEATURE [Part::Cylinder] Cylinder241  label="Cilindro241"
  Angle = 360
  Height = 10
  Placement = pos=(20,34.6,0) rot=(0,0,1;0rad)
  Radius = 2
FEATURE [Part::Cylinder] Cylinder242  label="Cilindro242"
  Angle = 360
  Height = 10
  Placement = pos=(25,43.3,0) rot=(0,0,1;0rad)
  Radius = 2
FEATURE [Part::Box] Box064  label="Cubo064"
  Height = 10
  Length = 23
  Width = 4
FEATURE [Part::Cylinder] Cylinder243  label="Cilindro243"
  Angle = 360
  Height = 10
  Placement = pos=(0,2,0) rot=(0,0,1;0rad)
  Radius = 2
FEATURE [Part::Cylinder] Cylinder244  label="Cilindro244"
  Angle = 360
  Height = 10
  Placement = pos=(23,2,0) rot=(0,0,1;0rad)
  Radius = 2
FEATURE [Part::MultiFuse] Fusion098
  Placement = pos=(3.5,60,0) rot=(0,0,1;0rad)
  Shapes = -> [Box064,Cylinder244,Cylinder243]
FEATURE [Part::Box] Box065  label="Cubo065"
  Height = 10
  Length = 23
  Width = 4
FEATURE [Part::Cylinder] Cylinder245  label="Cilindro245"
  Angle = 360
  Height = 10
  Placement = pos=(0,2,0) rot=(0,0,1;0rad)
  Radius = 2
FEATURE [Part::Cylinder] Cylinder246  label="Cilindro246"
  Angle = 360
  Height = 10
  Placement = pos=(23,2,0) rot=(0,0,1;0rad)
  Radius = 2
FEATURE [Part::MultiFuse] Fusion099
  Placement = pos=(-26.5,60,0) rot=(0,0,1;0rad)
  Shapes = -> [Box065,Cylinder246,Cylinder245]
FEATURE [Part::Box] Box066  label="Cubo066"
  Height = 10
  Length = 23
  Width = 4
FEATURE [Part::Cylinder] Cylinder247  label="Cilindro247"
  Angle = 360
  Height = 10
  Placement = pos=(0,2,0) rot=(0,0,1;0rad)
  Radius = 2
FEATURE [Part::Cylinder] Cylinder248  label="Cilindro248"
  Angle = 360
  Height = 10
  Placement = pos=(23,2,0) rot=(0,0,1;0rad)
  Radius = 2
FEATURE [Part::MultiFuse] Fusion100
  Placement = pos=(3.5,52,0) rot=(0,0,1;0rad)
  Shapes = -> [Box066,Cylinder248,Cylinder247]
FEATURE [Part::Box] Box067  label="Cubo067"
  Height = 10
  Length = 23
  Width = 4
FEATURE [Part::Cylinder] Cylinder249  label="Cilindro249"
  Angle = 360
  Height = 10
  Placement = pos=(0,2,0) rot=(0,0,1;0rad)
  Radius = 2
FEATURE [Part::Cylinder] Cylinder250  label="Cilindro250"
  Angle = 360
  Height = 10
  Placement = pos=(23,2,0) rot=(0,0,1;0rad)
  Radius = 2
FEATURE [Part::MultiFuse] Fusion101
  Placement = pos=(-26.5,52,0) rot=(0,0,1;0rad)
  Shapes = -> [Box067,Cylinder250,Cylinder249]
FEATURE [Part::MultiFuse] Fusion102
  Placement = pos=(0,0,-52) rot=(0,0,1;1.0472rad)
  Shapes = -> [Fusion100,Fusion101,Fusion099,Fusion098,Cylinder242,Cylinder241]
FEATURE [Part::Cylinder] Cylinder251  label="Cilindro251"
  Angle = 360
  Height = 10
  Placement = pos=(20,34.6,0) rot=(0,0,1;0rad)
  Radius = 2
FEATURE [Part::Cylinder] Cylinder252  label="Cilindro252"
  Angle = 360
  Height = 10
  Placement = pos=(25,43.3,0) rot=(0,0,1;0rad)
  Radius = 2
FEATURE [Part::Box] Box068  label="Cubo068"
  Height = 10
  Length = 23
  Width = 4
FEATURE [Part::Cylinder] Cylinder253  label="Cilindro253"
  Angle = 360
  Height = 10
  Placement = pos=(0,2,0) rot=(0,0,1;0rad)
  Radius = 2
FEATURE [Part::Cylinder] Cylinder254  label="Cilindro254"
  Angle = 360
  Height = 10
  Placement = pos=(23,2,0) rot=(0,0,1;0rad)
  Radius = 2
FEATURE [Part::MultiFuse] Fusion103
  Placement = pos=(3.5,60,0) rot=(0,0,1;0rad)
  Shapes = -> [Box068,Cylinder254,Cylinder253]
FEATURE [Part::Box] Box069  label="Cubo069"
  Height = 10
  Length = 23
  Width = 4
FEATURE [Part::Cylinder] Cylinder255  label="Cilindro255"
  Angle = 360
  Height = 10
  Placement = pos=(0,2,0) rot=(0,0,1;0rad)
  Radius = 2
FEATURE [Part::Cylinder] Cylinder256  label="Cilindro256"
  Angle = 360
  Height = 10
  Placement = pos=(23,2,0) rot=(0,0,1;0rad)
  Radius = 2
FEATURE [Part::MultiFuse] Fusion104
  Placement = pos=(-26.5,60,0) rot=(0,0,1;0rad)
  Shapes = -> [Box069,Cylinder256,Cylinder255]
FEATURE [Part::Box] Box070  label="Cubo070"
  Height = 10
  Length = 23
  Width = 4
FEATURE [Part::Cylinder] Cylinder257  label="Cilindro257"
  Angle = 360
  Height = 10
  Placement = pos=(0,2,0) rot=(0,0,1;0rad)
  Radius = 2
FEATURE [Part::Cylinder] Cylinder258  label="Cilindro258"
  Angle = 360
  Height = 10
  Placement = pos=(23,2,0) rot=(0,0,1;0rad)
  Radius = 2
FEATURE [Part::MultiFuse] Fusion105
  Placement = pos=(3.5,52,0) rot=(0,0,1;0rad)
  Shapes = -> [Box070,Cylinder258,Cylinder257]
FEATURE [Part::Box] Box071  label="Cubo071"
  Height = 10
  Length = 23
  Width = 4
FEATURE [Part::Cylinder] Cylinder259  label="Cilindro259"
  Angle = 360
  Height = 10
  Placement = pos=(0,2,0) rot=(0,0,1;0rad)
  Radius = 2
FEATURE [Part::Cylinder] Cylinder260  label="Cilindro260"
  Angle = 360
  Height = 10
  Placement = pos=(23,2,0) rot=(0,0,1;0rad)
  Radius = 2
FEATURE [Part::MultiFuse] Fusion106
  Placement = pos=(-26.5,52,0) rot=(0,0,1;0rad)
  Shapes = -> [Box071,Cylinder260,Cylinder259]
FEATURE [Part::MultiFuse] Fusion107
  Placement = pos=(0,0,-52) rot=(0,0,-1;2.0944rad)
  Shapes = -> [Fusion105,Fusion106,Fusion104,Fusion103,Cylinder252,Cylinder251]
FEATURE [Part::Cylinder] Cylinder261  label="Cilindro261"
  Angle = 360
  Height = 10
  Placement = pos=(20,34.6,0) rot=(0,0,1;0rad)
  Radius = 2
FEATURE [Part::Cylinder] Cylinder262  label="Cilindro262"
  Angle = 360
  Height = 10
  Placement = pos=(25,43.3,0) rot=(0,0,1;0rad)
  Radius = 2
FEATURE [Part::Box] Box072  label="Cubo072"
  Height = 10
  Length = 23
  Width = 4
FEATURE [Part::Cylinder] Cylinder263  label="Cilindro263"
  Angle = 360
  Height = 10
  Placement = pos=(0,2,0) rot=(0,0,1;0rad)
  Radius = 2
FEATURE [Part::Cylinder] Cylinder264  label="Cilindro264"
  Angle = 360
  Height = 10
  Placement = pos=(23,2,0) rot=(0,0,1;0rad)
  Radius = 2
FEATURE [Part::MultiFuse] Fusion108
  Placement = pos=(3.5,60,0) rot=(0,0,1;0rad)
  Shapes = -> [Box072,Cylinder264,Cylinder263]
FEATURE [Part::Box] Box073  label="Cubo073"
  Height = 10
  Length = 23
  Width = 4
FEATURE [Part::Cylinder] Cylinder265  label="Cilindro265"
  Angle = 360
  Height = 10
  Placement = pos=(0,2,0) rot=(0,0,1;0rad)
  Radius = 2
FEATURE [Part::Cylinder] Cylinder266  label="Cilindro266"
  Angle = 360
  Height = 10
  Placement = pos=(23,2,0) rot=(0,0,1;0rad)
  Radius = 2
FEATURE [Part::MultiFuse] Fusion109
  Placement = pos=(-26.5,60,0) rot=(0,0,1;0rad)
  Shapes = -> [Box073,Cylinder266,Cylinder265]
FEATURE [Part::Box] Box074  label="Cubo074"
  Height = 10
  Length = 23
  Width = 4
FEATURE [Part::Cylinder] Cylinder267  label="Cilindro267"
  Angle = 360
  Height = 10
  Placement = pos=(0,2,0) rot=(0,0,1;0rad)
  Radius = 2
FEATURE [Part::Cylinder] Cylinder268  label="Cilindro268"
  Angle = 360
  Height = 10
  Placement = pos=(23,2,0) rot=(0,0,1;0rad)
  Radius = 2
FEATURE [Part::MultiFuse] Fusion110
  Placement = pos=(3.5,52,0) rot=(0,0,1;0rad)
  Shapes = -> [Box074,Cylinder268,Cylinder267]
FEATURE [Part::Box] Box075  label="Cubo075"
  Height = 10
  Length = 23
  Width = 4
FEATURE [Part::Cylinder] Cylinder269  label="Cilindro269"
  Angle = 360
  Height = 10
  Placement = pos=(0,2,0) rot=(0,0,1;0rad)
  Radius = 2
FEATURE [Part::Cylinder] Cylinder270  label="Cilindro270"
  Angle = 360
  Height = 10
  Placement = pos=(23,2,0) rot=(0,0,1;0rad)
  Radius = 2
FEATURE [Part::MultiFuse] Fusion111
  Placement = pos=(-26.5,52,0) rot=(0,0,1;0rad)
  Shapes = -> [Box075,Cylinder270,Cylinder269]
FEATURE [Part::MultiFuse] Fusion112
  Placement = pos=(0,0,-52) rot=(0,0,-1;1.0472rad)
  Shapes = -> [Fusion110,Fusion111,Fusion109,Fusion108,Cylinder262,Cylinder261]
FEATURE [Part::Cylinder] Cylinder271  label="Cilindro271"
  Angle = 360
  Height = 10
  Placement = pos=(20,34.6,0) rot=(0,0,1;0rad)
  Radius = 2
FEATURE [Part::Cylinder] Cylinder272  label="Cilindro272"
  Angle = 360
  Height = 10
  Placement = pos=(25,43.3,0) rot=(0,0,1;0rad)
  Radius = 2
FEATURE [Part::Box] Box076  label="Cubo076"
  Height = 10
  Length = 23
  Width = 4
FEATURE [Part::Cylinder] Cylinder273  label="Cilindro273"
  Angle = 360
  Height = 10
  Placement = pos=(0,2,0) rot=(0,0,1;0rad)
  Radius = 2
FEATURE [Part::Cylinder] Cylinder274  label="Cilindro274"
  Angle = 360
  Height = 10
  Placement = pos=(23,2,0) rot=(0,0,1;0rad)
  Radius = 2
FEATURE [Part::MultiFuse] Fusion113
  Placement = pos=(3.5,60,0) rot=(0,0,1;0rad)
  Shapes = -> [Box076,Cylinder274,Cylinder273]
FEATURE [Part::Box] Box077  label="Cubo077"
  Height = 10
  Length = 23
  Width = 4
FEATURE [Part::Cylinder] Cylinder275  label="Cilindro275"
  Angle = 360
  Height = 10
  Placement = pos=(0,2,0) rot=(0,0,1;0rad)
  Radius = 2
FEATURE [Part::Cylinder] Cylinder276  label="Cilindro276"
  Angle = 360
  Height = 10
  Placement = pos=(23,2,0) rot=(0,0,1;0rad)
  Radius = 2
FEATURE [Part::MultiFuse] Fusion114
  Placement = pos=(-26.5,60,0) rot=(0,0,1;0rad)
  Shapes = -> [Box077,Cylinder276,Cylinder275]
FEATURE [Part::Box] Box078  label="Cubo078"
  Height = 10
  Length = 23
  Width = 4
FEATURE [Part::Cylinder] Cylinder277  label="Cilindro277"
  Angle = 360
  Height = 10
  Placement = pos=(0,2,0) rot=(0,0,1;0rad)
  Radius = 2
FEATURE [Part::Cylinder] Cylinder278  label="Cilindro278"
  Angle = 360
  Height = 10
  Placement = pos=(23,2,0) rot=(0,0,1;0rad)
  Radius = 2
FEATURE [Part::MultiFuse] Fusion115
  Placement = pos=(3.5,52,0) rot=(0,0,1;0rad)
  Shapes = -> [Box078,Cylinder278,Cylinder277]
FEATURE [Part::Box] Box079  label="Cubo079"
  Height = 10
  Length = 23
  Width = 4
FEATURE [Part::Cylinder] Cylinder279  label="Cilindro279"
  Angle = 360
  Height = 10
  Placement = pos=(0,2,0) rot=(0,0,1;0rad)
  Radius = 2
FEATURE [Part::Cylinder] Cylinder280  label="Cilindro280"
  Angle = 360
  Height = 10
  Placement = pos=(23,2,0) rot=(0,0,1;0rad)
  Radius = 2
FEATURE [Part::MultiFuse] Fusion116
  Placement = pos=(-26.5,52,0) rot=(0,0,1;0rad)
  Shapes = -> [Box079,Cylinder280,Cylinder279]
FEATURE [Part::MultiFuse] Fusion117
  Placement = pos=(0,0,-52) rot=(0,0,1;3.14159rad)
  Shapes = -> [Fusion115,Fusion116,Fusion114,Fusion113,Cylinder272,Cylinder271]
FEATURE [Part::Cylinder] Cylinder281  label="Cilindro281"
  Angle = 360
  Height = 10
  Placement = pos=(20,34.6,0) rot=(0,0,1;0rad)
  Radius = 2
FEATURE [Part::Cylinder] Cylinder282  label="Cilindro282"
  Angle = 360
  Height = 10
  Placement = pos=(25,43.3,0) rot=(0,0,1;0rad)
  Radius = 2
FEATURE [Part::Box] Box080  label="Cubo080"
  Height = 10
  Length = 23
  Width = 4
FEATURE [Part::Cylinder] Cylinder283  label="Cilindro283"
  Angle = 360
  Height = 10
  Placement = pos=(0,2,0) rot=(0,0,1;0rad)
  Radius = 2
FEATURE [Part::Cylinder] Cylinder284  label="Cilindro284"
  Angle = 360
  Height = 10
  Placement = pos=(23,2,0) rot=(0,0,1;0rad)
  Radius = 2
FEATURE [Part::MultiFuse] Fusion118
  Placement = pos=(3.5,60,0) rot=(0,0,1;0rad)
  Shapes = -> [Box080,Cylinder284,Cylinder283]
FEATURE [Part::Box] Box081  label="Cubo081"
  Height = 10
  Length = 23
  Width = 4
FEATURE [Part::Cylinder] Cylinder285  label="Cilindro285"
  Angle = 360
  Height = 10
  Placement = pos=(0,2,0) rot=(0,0,1;0rad)
  Radius = 2
FEATURE [Part::Cylinder] Cylinder286  label="Cilindro286"
  Angle = 360
  Height = 10
  Placement = pos=(23,2,0) rot=(0,0,1;0rad)
  Radius = 2
FEATURE [Part::MultiFuse] Fusion119
  Placement = pos=(-26.5,60,0) rot=(0,0,1;0rad)
  Shapes = -> [Box081,Cylinder286,Cylinder285]
FEATURE [Part::Box] Box082  label="Cubo082"
  Height = 10
  Length = 23
  Width = 4
FEATURE [Part::Cylinder] Cylinder287  label="Cilindro287"
  Angle = 360
  Height = 10
  Placement = pos=(0,2,0) rot=(0,0,1;0rad)
  Radius = 2
FEATURE [Part::Cylinder] Cylinder288  label="Cilindro288"
  Angle = 360
  Height = 10
  Placement = pos=(23,2,0) rot=(0,0,1;0rad)
  Radius = 2
FEATURE [Part::MultiFuse] Fusion120
  Placement = pos=(3.5,52,0) rot=(0,0,1;0rad)
  Shapes = -> [Box082,Cylinder288,Cylinder287]
FEATURE [Part::Box] Box083  label="Cubo083"
  Height = 10
  Length = 23
  Width = 4
FEATURE [Part::Cylinder] Cylinder289  label="Cilindro289"
  Angle = 360
  Height = 10
  Placement = pos=(0,2,0) rot=(0,0,1;0rad)
  Radius = 2
FEATURE [Part::Cylinder] Cylinder290  label="Cilindro290"
  Angle = 360
  Height = 10
  Placement = pos=(23,2,0) rot=(0,0,1;0rad)
  Radius = 2
FEATURE [Part::MultiFuse] Fusion121
  Placement = pos=(-26.5,52,0) rot=(0,0,1;0rad)
  Shapes = -> [Box083,Cylinder290,Cylinder289]
FEATURE [Part::MultiFuse] Fusion122
  Placement = pos=(0,0,-52) rot=(0,0,1;2.0944rad)
  Shapes = -> [Fusion120,Fusion121,Fusion119,Fusion118,Cylinder282,Cylinder281]
FEATURE [Part::MultiFuse] Fusion123
  Shapes = -> [Fusion122,Fusion117,Fusion112,Fusion107,Fusion102,Fusion097]
FEATURE [Part::Cut] Cut006
  Base = -> Extrude005
  Tool = -> Fusion123
FEATURE [Part::Cylinder] Cylinder291  label="Cilindro291"
  Angle = 360
  Height = 10
  Placement = pos=(-39.5,-25.5,-60) rot=(0,0,1;0rad)
  Radius = 1.5
FEATURE [Part::Cylinder] Cylinder292  label="Cilindro292"
  Angle = 360
  Height = 10
  Placement = pos=(-39.5,23.5,-60) rot=(0,0,1;0rad)
  Radius = 1.5
FEATURE [Part::Cylinder] Cylinder293  label="Cilindro293"
  Angle = 360
  Height = 10
  Placement = pos=(18.5,-25.5,-60) rot=(0,0,1;0rad)
  Radius = 1.5
FEATURE [Part::Cylinder] Cylinder294  label="Cilindro294"
  Angle = 360
  Height = 10
  Placement = pos=(18.5,23.5,-60) rot=(0,0,1;0rad)
  Radius = 1.5
FEATURE [Part::MultiFuse] Fusion124
  Placement = pos=(0,0,7) rot=(0,0,1;0rad)
  Shapes = -> [Cylinder294,Cylinder293,Cylinder292,Cylinder291]
FEATURE [Part::Cut] Cut007
  Base = -> Cut006
  Placement = pos=(0,0,0) rot=(1,0,0;3.14159rad)
  Tool = -> Fusion124
FEATURE [Part::Cylinder] Cylinder295  label="Cilindro295"
  Angle = 360
  Height = 2
  Radius = 1.45
FEATURE [Part::Cylinder] Cylinder296  label="Cilindro296"
  Angle = 360
  Height = 2
  Radius = 3.2
FEATURE [Part::Box] Box084  label="Cubo084"
  Height = 2
  Length = 8
  Placement = pos=(-8,-3.2,0) rot=(0,0,1;0rad)
  Width = 6.4
FEATURE [Part::MultiFuse] Fusion125
  Shapes = -> [Cylinder296,Box084]
FEATURE [Part::Cut] Cut008
  Base = -> Fusion125
  Placement = pos=(-39.5,-23.5,61.6) rot=(0,0,1;0rad)
  Tool = -> Cylinder295
FEATURE [Part::Cylinder] Cylinder297  label="Cilindro297"
  Angle = 360
  Height = 2
  Radius = 1.45
FEATURE [Part::Cylinder] Cylinder298  label="Cilindro298"
  Angle = 360
  Height = 2
  Radius = 3.2
FEATURE [Part::Box] Box085  label="Cubo085"
  Height = 2
  Length = 8
  Placement = pos=(-8,-3.2,0) rot=(0,0,1;0rad)
  Width = 6.4
FEATURE [Part::MultiFuse] Fusion126
  Shapes = -> [Cylinder298,Box085]
FEATURE [Part::Cut] Cut009
  Base = -> Fusion126
  Placement = pos=(-39.5,25.5,61.6) rot=(0,0,1;0rad)
  Tool = -> Cylinder297
FEATURE [Part::Box] Box086  label="Cubo086"
  Height = 26
  Length = 4
  Placement = pos=(-47.5,-26.7,61.6) rot=(0,0,1;0rad)
  Width = 55.4
FEATURE [Part::MultiFuse] Fusion127
  Shapes = -> [Cut008,Cut009,Box086]
FEATURE [Part::Chamfer] Chamfer
  Base = -> Fusion127
  Edges = 2 edges r=1: [Edge15,Edge19]
FEATURE [Part::Box] Box087  label="Cubo087"
  Height = 5
  Length = 14
  Placement = pos=(-43,-14,76) rot=(0,-1,0;1.5708rad)
  Width = 30
FEATURE [Part::Box] Box088  label="Cubo088"
  Height = 1.8
  Length = 25
  Placement = pos=(-44,-10.2,76) rot=(0,-1,0;1.5708rad)
  Width = 24
FEATURE [Part::Box] Box089  label="Cubo089"
  Height = 10
  Length = 25
  Placement = pos=(-41,-8.7,76) rot=(0,-1,0;1.5708rad)
  Width = 21
FEATURE [Part::MultiFuse] Fusion128
  Placement = pos=(-0.5,-0.7,0) rot=(0,0,1;0rad)
  Shapes = -> [Box089,Box088]
FEATURE [Part::MultiFuse] Fusion129
  Shapes = -> [Box087,Chamfer]
FEATURE [Part::Cut] Cut010
  Base = -> Fusion129
  Tool = -> Fusion128
FEATURE [Part::Chamfer] Chamfer001
  Base = -> Cut010
  Edges = 2 edges r=8: [Edge65,Edge92]
FEATURE [Part::Fillet] Fillet
  Base = -> Chamfer001
  Edges = 4 edges r=1: [Edge23,Edge28,Edge69,Edge71]
FEATURE [Part::Fillet] Fillet001
  Base = -> Fillet
  Edges = 2 edges r=1: [Edge45,Edge74]
FEATURE [Part::Chamfer] Chamfer002
  Base = -> Fillet001
  Edges = 2 edges r=1: [Edge116,Edge145]
FEATURE [Part::Chamfer] Chamfer003
  Base = -> Chamfer002
  Edges = 4 edges r=1: [Edge2,Edge7,Edge156,Edge160]
FEATURE [Part::Chamfer] Chamfer004
  Base = -> Chamfer003
  Edges = 4 edges r=0.45: [Edge46,Edge52,Edge56,Edge77]
